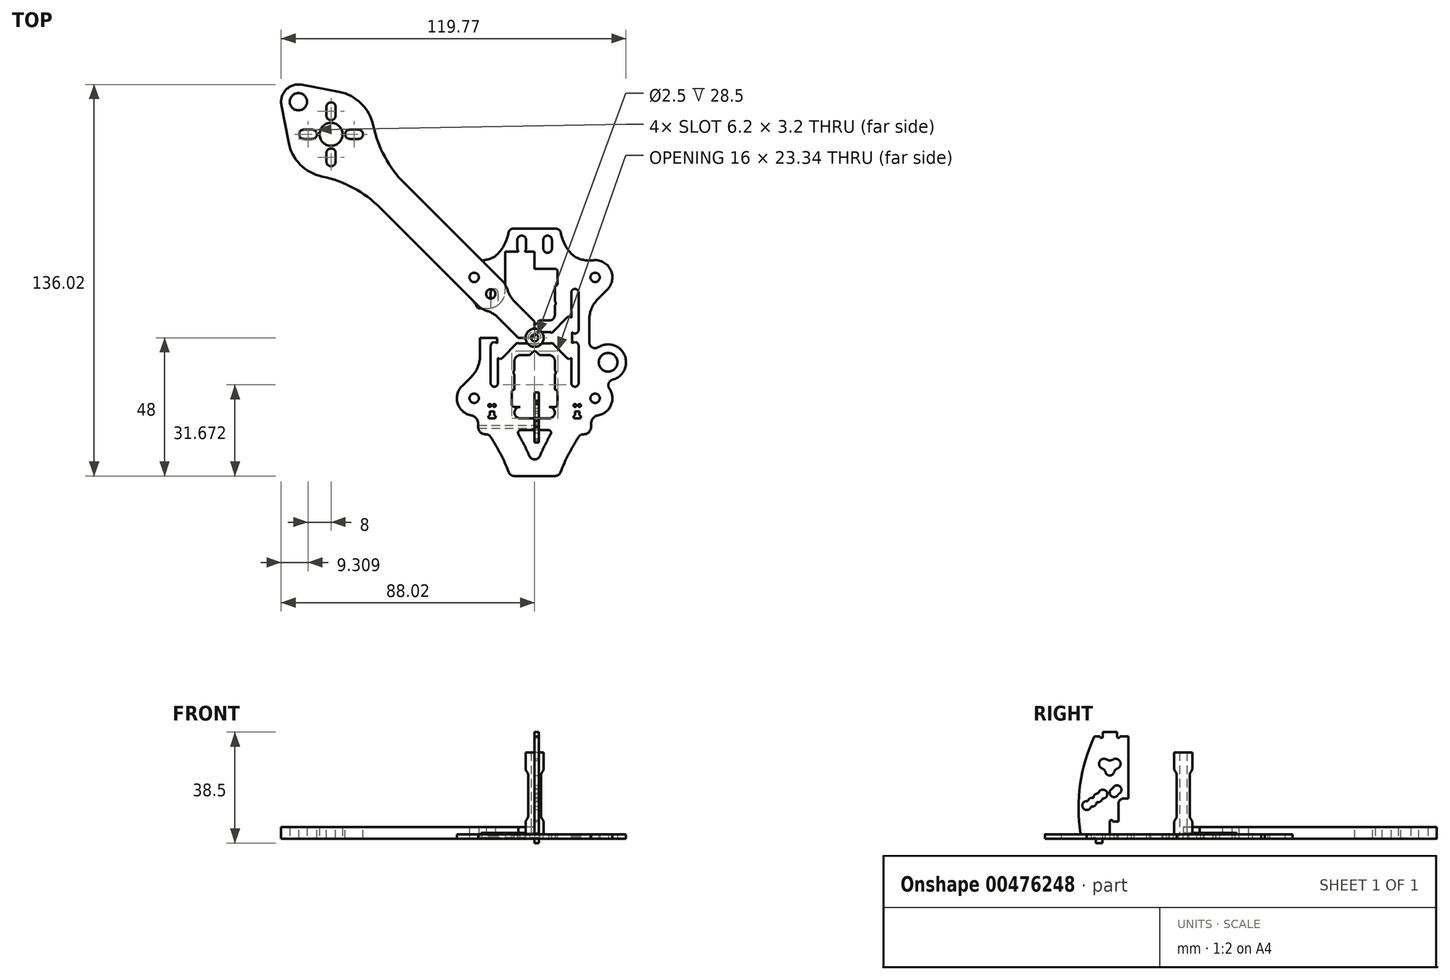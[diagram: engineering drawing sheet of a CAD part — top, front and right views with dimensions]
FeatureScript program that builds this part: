
annotation { "Feature Type Name" : "Feature", "Feature Type Description" : "" }
export const myFeature = defineFeature(function(context is Context, id is Id, definition is map)
    precondition{}
    {
        {
            var Q0;
            Q0=qCreatedBy(makeId("Top.planeOp"),FACE);
            var sketch = newSketch(context, id + "F0", { "sketchPlane" : qUnion([Q0])});
            skCircle(sketch, "E0", {"center": v(-15.25, 15.25) * mm, "radius": 2.23 * mm});
            skCircle(sketch, "E1", {"center": v(15.25, 15.25) * mm, "radius": 2.23 * mm});
            skCircle(sketch, "E2", {"center": v(15.25, -15.25) * mm, "radius": 2.23 * mm});
            skCircle(sketch, "E3", {"center": v(-15.25, -15.25) * mm, "radius": 2.23 * mm});
            skCircle(sketch, "E4", {"center": v(-21, 21) * mm, "radius": 1.63 * mm});
            skCircle(sketch, "E5.MirrorC", {"center": v(21, 21) * mm, "radius": 1.63 * mm});
            skCircle(sketch, "E6.MirrorC", {"center": v(-21, -21) * mm, "radius": 1.63 * mm});
            skCircle(sketch, "E7.MirrorC", {"center": v(21, -21) * mm, "radius": 1.63 * mm});
            skArc(sketch, "E8", {"start": v(-16.76, 25.24) * mm, "mid": v(-25.24, 25.24) * mm, "end": v(-25.24, 16.76) * mm});
            skLineSegment(sketch, "E9", {"start": v(-16.76, 25.24) * mm, "end": v(-15.56, 24.04) * mm});
            skLineSegment(sketch, "E10", {"start": v(-25.24, 16.76) * mm, "end": v(-21.93, 13.44) * mm});
            skLineSegment(sketch, "E11.MirrorCS", {"start": v(-25.24, -16.76) * mm, "end": v(-21.93, -13.44) * mm});
            skArc(sketch, "E12.MirrorCS", {"start": v(-16.76, -25.24) * mm, "mid": v(-25.24, -25.24) * mm, "end": v(-25.24, -16.76) * mm});
            skLineSegment(sketch, "E13.MirrorCS", {"start": v(-16.76, -25.24) * mm, "end": v(-15.56, -24.04) * mm});
            skLineSegment(sketch, "E14.MirrorCS", {"start": v(16.76, 25.24) * mm, "end": v(15.56, 24.04) * mm});
            skArc(sketch, "E15.MirrorCS", {"start": v(16.76, 25.24) * mm, "mid": v(25.24, 25.24) * mm, "end": v(25.24, 16.76) * mm});
            skLineSegment(sketch, "E16.MirrorCS", {"start": v(25.24, 16.76) * mm, "end": v(21.93, 13.44) * mm});
            skLineSegment(sketch, "E17.MirrorCS", {"start": v(25.24, -16.76) * mm, "end": v(21.93, -13.44) * mm});
            skArc(sketch, "E18.MirrorCS", {"start": v(16.76, -25.24) * mm, "mid": v(25.24, -25.24) * mm, "end": v(25.24, -16.76) * mm});
            skLineSegment(sketch, "E19.MirrorCS", {"start": v(16.76, -25.24) * mm, "end": v(15.56, -24.04) * mm});
            skPoint(sketch, "E20.visualSharp", {"position": v(0, 8.49) * mm});
            skPoint(sketch, "E21.visualSharp", {"position": v(0, -8.49) * mm});
            skArc(sketch, "E21.filletArc", {"start": v(15.56, -24.04) * mm, "mid": v(0, -17.6) * mm, "end": v(-15.56, -24.04) * mm});
            skLineSegment(sketch, "E22", {"start": v(-21, 21) * mm, "end": v(0, 0) * mm, "construction": true});
            skArc(sketch, "E23.filletArc", {"start": v(-15.56, 24.04) * mm, "mid": v(0, 17.6) * mm, "end": v(15.56, 24.04) * mm});
            skLineSegment(sketch, "E24", {"start": v(-19, 6.37) * mm, "end": v(-19, -6.37) * mm});
            skLineSegment(sketch, "E25.MirrorCS", {"start": v(19, 6.37) * mm, "end": v(19, -6.37) * mm});
            skLineSegment(sketch, "E26", {"start": v(0, 0) * mm, "end": v(21, -21) * mm, "construction": true});
            skLineSegment(sketch, "E27", {"start": v(21, 21) * mm, "end": v(-21, -21) * mm, "construction": true});
            skLineSegment(sketch, "E28.0", {"start": v(0.7, -7.78) * mm, "end": v(5.22, -12.3) * mm});
            skLineSegment(sketch, "E28.1", {"start": v(-12.3, 5.22) * mm, "end": v(-7.78, 0.7) * mm});
            skLineSegment(sketch, "E29.0", {"start": v(-5.22, 12.3) * mm, "end": v(-0.7, 7.78) * mm});
            skLineSegment(sketch, "E30.0", {"start": v(7.78, -0.7) * mm, "end": v(12.3, -5.22) * mm});
            skLineSegment(sketch, "E31.MirrorCS", {"start": v(5.22, 12.3) * mm, "end": v(0.7, 7.78) * mm});
            skLineSegment(sketch, "E32.MirrorCS", {"start": v(12.3, 5.22) * mm, "end": v(7.78, 0.7) * mm});
            skLineSegment(sketch, "E33.MirrorCS", {"start": v(-0.7, -7.78) * mm, "end": v(-5.22, -12.3) * mm});
            skLineSegment(sketch, "E34.MirrorCS", {"start": v(-7.78, -0.7) * mm, "end": v(-12.3, -5.22) * mm});
            skPoint(sketch, "E35.orphan", {"position": v(-3.54, -3.54) * mm});
            skPoint(sketch, "E36.orphan", {"position": v(3.54, -3.54) * mm});
            skLineSegment(sketch, "E37", {"start": v(-4.51, 14) * mm, "end": v(4.51, 14) * mm});
            skLineSegment(sketch, "E38", {"start": v(-14, 4.51) * mm, "end": v(-14, -4.51) * mm});
            skLineSegment(sketch, "E39", {"start": v(-4.51, -14) * mm, "end": v(4.51, -14) * mm});
            skLineSegment(sketch, "E40", {"start": v(14, -4.51) * mm, "end": v(14, 4.51) * mm});
            skPoint(sketch, "E41.visualSharp", {"position": v(-14, 6.93) * mm});
            skArc(sketch, "E41.filletArc", {"start": v(-12.3, 5.22) * mm, "mid": v(-13.38, 5.44) * mm, "end": v(-14, 4.51) * mm});
            skPoint(sketch, "E42.visualSharp", {"position": v(-14, -6.93) * mm});
            skArc(sketch, "E42.filletArc", {"start": v(-14, -4.51) * mm, "mid": v(-13.38, -5.44) * mm, "end": v(-12.3, -5.22) * mm});
            skPoint(sketch, "E43.visualSharp", {"position": v(-7.07, 0) * mm});
            skArc(sketch, "E43.filletArc", {"start": v(-7.78, -0.7) * mm, "mid": v(-7.49, 0) * mm, "end": v(-7.78, 0.7) * mm});
            skPoint(sketch, "E44.visualSharp", {"position": v(0, -7.07) * mm});
            skArc(sketch, "E44.filletArc", {"start": v(0.7, -7.78) * mm, "mid": v(0, -7.49) * mm, "end": v(-0.7, -7.78) * mm});
            skPoint(sketch, "E45.visualSharp", {"position": v(-6.93, -14) * mm});
            skArc(sketch, "E45.filletArc", {"start": v(-5.22, -12.3) * mm, "mid": v(-5.44, -13.38) * mm, "end": v(-4.51, -14) * mm});
            skPoint(sketch, "E46.visualSharp", {"position": v(6.93, -14) * mm});
            skArc(sketch, "E46.filletArc", {"start": v(4.51, -14) * mm, "mid": v(5.44, -13.38) * mm, "end": v(5.22, -12.3) * mm});
            skPoint(sketch, "E47.visualSharp", {"position": v(14, -6.93) * mm});
            skArc(sketch, "E47.filletArc", {"start": v(12.3, -5.22) * mm, "mid": v(13.38, -5.44) * mm, "end": v(14, -4.51) * mm});
            skPoint(sketch, "E48.visualSharp", {"position": v(14, 6.93) * mm});
            skArc(sketch, "E48.filletArc", {"start": v(14, 4.51) * mm, "mid": v(13.38, 5.44) * mm, "end": v(12.3, 5.22) * mm});
            skPoint(sketch, "E49.visualSharp", {"position": v(7.07, 0) * mm});
            skArc(sketch, "E49.filletArc", {"start": v(7.78, 0.7) * mm, "mid": v(7.49, 0) * mm, "end": v(7.78, -0.7) * mm});
            skPoint(sketch, "E50.visualSharp", {"position": v(0, 7.07) * mm});
            skArc(sketch, "E50.filletArc", {"start": v(-0.7, 7.78) * mm, "mid": v(0, 7.49) * mm, "end": v(0.7, 7.78) * mm});
            skPoint(sketch, "E51.visualSharp", {"position": v(-6.93, 14) * mm});
            skArc(sketch, "E51.filletArc", {"start": v(-4.51, 14) * mm, "mid": v(-5.44, 13.38) * mm, "end": v(-5.22, 12.3) * mm});
            skPoint(sketch, "E52.visualSharp", {"position": v(6.93, 14) * mm});
            skArc(sketch, "E52.filletArc", {"start": v(5.22, 12.3) * mm, "mid": v(5.44, 13.38) * mm, "end": v(4.51, 14) * mm});
            skPoint(sketch, "E53.visualSharp", {"position": v(-19, 10.51) * mm});
            skArc(sketch, "E53.filletArc", {"start": v(-19, 6.37) * mm, "mid": v(-19.76, 10.2) * mm, "end": v(-21.93, 13.44) * mm});
            skPoint(sketch, "E54.visualSharp", {"position": v(-19, -10.51) * mm});
            skArc(sketch, "E54.filletArc", {"start": v(-21.93, -13.44) * mm, "mid": v(-19.76, -10.2) * mm, "end": v(-19, -6.37) * mm});
            skPoint(sketch, "E55.visualSharp", {"position": v(19, -10.51) * mm});
            skArc(sketch, "E55.filletArc", {"start": v(19, -6.37) * mm, "mid": v(19.76, -10.2) * mm, "end": v(21.93, -13.44) * mm});
            skPoint(sketch, "E56.visualSharp", {"position": v(19, 10.51) * mm});
            skArc(sketch, "E56.filletArc", {"start": v(21.93, 13.44) * mm, "mid": v(19.76, 10.2) * mm, "end": v(19, 6.37) * mm});
            skSolve(sketch);
        }
        {
            var Q0;
            Q0=makeQuery(id+"F0.imprint","IMPRINT",FACE,{"disambiguationData":[TD([[makeQuery(id+"F0.imprint","IMPRINT",EDGE,{"derivedFrom":sQuery(id+"F0.wireOp",EDGE,"E0")}),-1.0]])]});
            extrude(context, id + "F1", {"entities" : qUnion([Q0]), "depth" : 1.5 * mm, "offsetDistance" : 25 * mm});
        }
        {
            var Q0;
            Q0=qCreatedBy(makeId("Top.planeOp"),FACE);
            var sketch = newSketch(context, id + "F2", { "sketchPlane" : qUnion([Q0])});
            skCircle(sketch, "E57", {"center": v(-15.25, 15.25) * mm, "radius": 1.63 * mm});
            skCircle(sketch, "E58", {"center": v(-21, 21) * mm, "radius": 1.63 * mm});
            skArc(sketch, "E59", {"start": v(-20.23, 26.95) * mm, "mid": v(-26.38, 23.65) * mm, "end": v(-25.24, 16.76) * mm});
            skLineSegment(sketch, "E60", {"start": v(-18, 7.44) * mm, "end": v(-18, 0) * mm});
            skPoint(sketch, "E61.visualSharp", {"position": v(-18, 10) * mm});
            skLineSegment(sketch, "E62", {"start": v(0, 38) * mm, "end": v(0, -38) * mm, "construction": true});
            skLineSegment(sketch, "E63.MirrorCS", {"start": v(18, 7.44) * mm, "end": v(18, 0) * mm});
            skArc(sketch, "E64.MirrorCS", {"start": v(20.23, 26.95) * mm, "mid": v(26.38, 23.65) * mm, "end": v(25.24, 16.76) * mm});
            skCircle(sketch, "E65.MirrorC", {"center": v(21, 21) * mm, "radius": 1.63 * mm});
            skCircle(sketch, "E66.MirrorC", {"center": v(15.25, 15.25) * mm, "radius": 1.63 * mm});
            skPoint(sketch, "E67.MirrorP", {"position": v(18, 10) * mm});
            skPoint(sketch, "E68.MirrorP", {"position": v(18, -10) * mm});
            skLineSegment(sketch, "E69.MirrorCS", {"start": v(18, -7.44) * mm, "end": v(18, 0) * mm});
            skLineSegment(sketch, "E70.MirrorCS", {"start": v(-18, -7.44) * mm, "end": v(-18, 0) * mm});
            skPoint(sketch, "E71.MirrorP", {"position": v(-18, -10) * mm});
            skCircle(sketch, "E72.MirrorC", {"center": v(-15.25, -15.25) * mm, "radius": 1.63 * mm});
            skCircle(sketch, "E73.MirrorC", {"center": v(-21, -21) * mm, "radius": 1.63 * mm});
            skArc(sketch, "E74.MirrorCS", {"start": v(-22.07, -26.9) * mm, "mid": v(-26.73, -22.8) * mm, "end": v(-25.24, -16.76) * mm});
            skCircle(sketch, "E75.MirrorC", {"center": v(21, -21) * mm, "radius": 1.63 * mm});
            skCircle(sketch, "E76.MirrorC", {"center": v(15.25, -15.25) * mm, "radius": 1.63 * mm});
            skArc(sketch, "E77.MirrorCS", {"start": v(22.07, -26.9) * mm, "mid": v(26.73, -22.8) * mm, "end": v(25.24, -16.76) * mm});
            skLineSegment(sketch, "E78.bottom", {"start": v(-15.6, -25.5) * mm, "end": v(-14, -25.5) * mm});
            skLineSegment(sketch, "E78.top", {"start": v(-15.6, -30.5) * mm, "end": v(-14, -30.5) * mm});
            skLineSegment(sketch, "E78.left", {"start": v(-15.6, -25.5) * mm, "end": v(-15.6, -30.5) * mm});
            skLineSegment(sketch, "E78.right", {"start": v(-14, -25.5) * mm, "end": v(-14, -30.5) * mm});
            skLineSegment(sketch, "E79.MirrorCS", {"start": v(15.6, -25.5) * mm, "end": v(14, -25.5) * mm});
            skLineSegment(sketch, "E80.MirrorCS", {"start": v(15.6, -25.5) * mm, "end": v(15.6, -30.5) * mm});
            skLineSegment(sketch, "E81.MirrorCS", {"start": v(14, -25.5) * mm, "end": v(14, -30.5) * mm});
            skLineSegment(sketch, "E82.MirrorCS", {"start": v(15.6, -30.5) * mm, "end": v(14, -30.5) * mm});
            skLineSegment(sketch, "E83", {"start": v(-25.24, -16.76) * mm, "end": v(-25.24, -16.76) * mm});
            skLineSegment(sketch, "E84", {"start": v(-21, -21) * mm, "end": v(0, 0) * mm, "construction": true});
            skLineSegment(sketch, "E85", {"start": v(-19.6, -29.86) * mm, "end": v(-19.6, -31) * mm});
            skLineSegment(sketch, "E86", {"start": v(-17.1, -33.5) * mm, "end": v(-16.97, -33.5) * mm});
            skLineSegment(sketch, "E87.MirrorCS", {"start": v(19.6, -29.86) * mm, "end": v(19.6, -31) * mm});
            skLineSegment(sketch, "E88.MirrorCS", {"start": v(17.1, -33.5) * mm, "end": v(16.97, -33.5) * mm});
            skLineSegment(sketch, "E89", {"start": v(-25.24, 16.76) * mm, "end": v(-19.46, 10.98) * mm});
            skLineSegment(sketch, "E90", {"start": v(0, 0) * mm, "end": v(-15.25, 15.25) * mm, "construction": true});
            skLineSegment(sketch, "E91.MirrorCS", {"start": v(-25.24, -16.76) * mm, "end": v(-19.46, -10.98) * mm});
            skLineSegment(sketch, "E92.MirrorCS", {"start": v(25.24, 16.76) * mm, "end": v(19.46, 10.98) * mm});
            skLineSegment(sketch, "E93.MirrorCS", {"start": v(25.24, -16.76) * mm, "end": v(19.46, -10.98) * mm});
            skLineSegment(sketch, "E94", {"start": v(-21, -21) * mm, "end": v(-70.71, -70.71) * mm, "construction": true});
            skCircle(sketch, "E95", {"center": v(-70.71, -70.71) * mm, "radius": 64.25 * mm, "construction": true});
            skArc(sketch, "E96", {"start": v(-8.47, -48) * mm, "mid": v(-11.5, -41) * mm, "end": v(-15.3, -34.4) * mm});
            skLineSegment(sketch, "E97", {"start": v(-8.47, -48) * mm, "end": v(0, -48) * mm});
            skArc(sketch, "E98.MirrorCS", {"start": v(8.47, -48) * mm, "mid": v(11.5, -41) * mm, "end": v(15.3, -34.4) * mm});
            skLineSegment(sketch, "E99.MirrorCS", {"start": v(8.47, -48) * mm, "end": v(0, -48) * mm});
            skArc(sketch, "E100", {"start": v(-20.23, 26.95) * mm, "mid": v(-12.61, 29.12) * mm, "end": v(-8.96, 36.14) * mm});
            skArc(sketch, "E101.MirrorCS", {"start": v(20.23, 26.95) * mm, "mid": v(12.61, 29.12) * mm, "end": v(8.96, 36.14) * mm});
            skPoint(sketch, "E102.visualSharp", {"position": v(-15.9, -33.5) * mm});
            skArc(sketch, "E102.filletArc", {"start": v(-15.3, -34.4) * mm, "mid": v(-16.02, -33.74) * mm, "end": v(-16.97, -33.5) * mm});
            skPoint(sketch, "E103.visualSharp", {"position": v(15.9, -33.5) * mm});
            skArc(sketch, "E103.filletArc", {"start": v(16.97, -33.5) * mm, "mid": v(16.02, -33.74) * mm, "end": v(15.3, -34.4) * mm});
            skLineSegment(sketch, "E104", {"start": v(-6.97, 38) * mm, "end": v(6.97, 38) * mm});
            skPoint(sketch, "E105.orphan", {"position": v(-8.47, 48) * mm});
            skPoint(sketch, "E106.orphan", {"position": v(8.47, 48) * mm});
            skPoint(sketch, "E107.visualSharp", {"position": v(-9, 38) * mm});
            skArc(sketch, "E107.filletArc", {"start": v(-6.97, 38) * mm, "mid": v(-8.33, 37.46) * mm, "end": v(-8.96, 36.14) * mm});
            skPoint(sketch, "E108.visualSharp", {"position": v(9, 38) * mm});
            skArc(sketch, "E108.filletArc", {"start": v(8.96, 36.14) * mm, "mid": v(8.33, 37.46) * mm, "end": v(6.97, 38) * mm});
            skPoint(sketch, "E109.visualSharp", {"position": v(-18, 9.51) * mm});
            skArc(sketch, "E109.filletArc", {"start": v(-18, 7.44) * mm, "mid": v(-18.38, 9.36) * mm, "end": v(-19.46, 10.98) * mm});
            skPoint(sketch, "E110.visualSharp", {"position": v(-18, -9.51) * mm});
            skArc(sketch, "E110.filletArc", {"start": v(-19.46, -10.98) * mm, "mid": v(-18.38, -9.36) * mm, "end": v(-18, -7.44) * mm});
            skPoint(sketch, "E111.visualSharp", {"position": v(18, 9.51) * mm});
            skArc(sketch, "E111.filletArc", {"start": v(19.46, 10.98) * mm, "mid": v(18.38, 9.36) * mm, "end": v(18, 7.44) * mm});
            skPoint(sketch, "E112.visualSharp", {"position": v(18, -9.51) * mm});
            skArc(sketch, "E112.filletArc", {"start": v(18, -7.44) * mm, "mid": v(18.38, -9.36) * mm, "end": v(19.46, -10.98) * mm});
            skArc(sketch, "E113", {"start": v(-19.6, -29.86) * mm, "mid": v(-20.3, -27.93) * mm, "end": v(-22.07, -26.9) * mm});
            skPoint(sketch, "E114.visualSharp", {"position": v(-19.6, -33.5) * mm});
            skArc(sketch, "E114.filletArc", {"start": v(-19.6, -31) * mm, "mid": v(-18.87, -32.77) * mm, "end": v(-17.1, -33.5) * mm});
            skArc(sketch, "E115.MirrorCS", {"start": v(19.6, -29.86) * mm, "mid": v(20.3, -27.93) * mm, "end": v(22.07, -26.9) * mm});
            skPoint(sketch, "E116.visualSharp", {"position": v(19.6, -33.5) * mm});
            skArc(sketch, "E116.filletArc", {"start": v(17.1, -33.5) * mm, "mid": v(18.87, -32.77) * mm, "end": v(19.6, -31) * mm});
            skSolve(sketch);
        }
        {
            var Q0;
            Q0=makeQuery(id+"F2.imprint","IMPRINT",FACE,{"disambiguationData":[TD([[makeQuery(id+"F2.imprint","IMPRINT",EDGE,{"derivedFrom":sQuery(id+"F2.wireOp",EDGE,"E57")}),-1.0]])]});
            extrude(context, id + "F3", {"entities" : qUnion([Q0]), "depth" : 1.5 * mm});
        }
        {
            var Q0;
            Q0=makeQuery(id+"F3.opExtrude","CAP_FACE",FACE,{"disambiguationData":[OSD([sQuery(id+"F2.wireOp",EDGE,"E57"),sQuery(id+"F2.wireOp",EDGE,"jFPTTxz4-jLXj-DDCv-FC09-USVAbM95QFUD"),sQuery(id+"F2.wireOp",EDGE,"E58"),sQuery(id+"F2.wireOp",EDGE,"E59"),sQuery(id+"F2.wireOp",EDGE,"E60"),sQuery(id+"F2.wireOp",EDGE,"OV2Wl9yg-sUyD-2Hj2-rkXj-MTIEYF9VZsJK"),sQuery(id+"F2.wireOp",EDGE,"91e39d24-f0d0-409c-99ef-685c742f9300.filletArc"),sQuery(id+"F2.wireOp",EDGE,"E61.filletArc"),sQuery(id+"F2.wireOp",EDGE,"2RSG9yHZ-WQqx-c2xK-pqDh-UdEIjaxC7IlA"),sQuery(id+"F2.wireOp",EDGE,"4rgxPuH5-7xbP-ZsFa-2w6e-7YXQlRziYjOP"),sQuery(id+"F2.wireOp",EDGE,"aAb2sQRX-3QeW-SLoE-m21K-AacbavdIfjy6"),sQuery(id+"F2.wireOp",EDGE,"7c283ec5-88dc-4330-9acd-45fa73696fd10.MirrorCS"),sQuery(id+"F2.wireOp",EDGE,"7c283ec5-88dc-4330-9acd-45fa73696fd11.MirrorCS"),sQuery(id+"F2.wireOp",EDGE,"E63.MirrorCS"),sQuery(id+"F2.wireOp",EDGE,"E64.MirrorCS"),sQuery(id+"F2.wireOp",EDGE,"E65.MirrorC"),sQuery(id+"F2.wireOp",EDGE,"7c283ec5-88dc-4330-9acd-45fa73696fd112.MirrorC"),sQuery(id+"F2.wireOp",EDGE,"E66.MirrorC"),sQuery(id+"F2.wireOp",EDGE,"7c283ec5-88dc-4330-9acd-45fa73696fd114.MirrorCS"),sQuery(id+"F2.wireOp",EDGE,"7c283ec5-88dc-4330-9acd-45fa73696fd116.MirrorCS"),sQuery(id+"F2.wireOp",EDGE,"77becaeb-8b8b-4dc1-b250-45090536f0a20.MirrorCS"),sQuery(id+"F2.wireOp",EDGE,"26ce58a3-4cb5-4f15-a1e7-5b8d20efb5c40.MirrorCS"),sQuery(id+"F2.wireOp",EDGE,"9822711c-84ae-4c2d-bbd4-b3a60979fe173.MirrorCS"),sQuery(id+"F2.wireOp",EDGE,"9822711c-84ae-4c2d-bbd4-b3a60979fe174.MirrorCS"),sQuery(id+"F2.wireOp",EDGE,"E69.MirrorCS"),sQuery(id+"F2.wireOp",EDGE,"9822711c-84ae-4c2d-bbd4-b3a60979fe176.MirrorCS"),sQuery(id+"F2.wireOp",EDGE,"4a2114cf-ddcc-4bd1-b273-f588f7a722dc0.MirrorCS"),sQuery(id+"F2.wireOp",EDGE,"4a2114cf-ddcc-4bd1-b273-f588f7a722dc1.MirrorCS"),sQuery(id+"F2.wireOp",EDGE,"4a2114cf-ddcc-4bd1-b273-f588f7a722dc2.MirrorCS"),sQuery(id+"F2.wireOp",EDGE,"E70.MirrorCS"),sQuery(id+"F2.wireOp",EDGE,"E72.MirrorC"),sQuery(id+"F2.wireOp",EDGE,"E73.MirrorC"),sQuery(id+"F2.wireOp",EDGE,"E74.MirrorCS"),sQuery(id+"F2.wireOp",EDGE,"E75.MirrorC"),sQuery(id+"F2.wireOp",EDGE,"E76.MirrorC"),sQuery(id+"F2.wireOp",EDGE,"5bfa031d-9f72-4db7-bc0c-70e661b370ed0.MirrorC"),sQuery(id+"F2.wireOp",EDGE,"6425a8bc-ce2c-4a8b-8028-989707d169630.MirrorC"),sQuery(id+"F2.wireOp",EDGE,"E77.MirrorCS"),sQuery(id+"F2.wireOp",EDGE,"b8184357-9e1d-4d76-b8cc-bd6e0700e5e00.MirrorCS"),sQuery(id+"F2.wireOp",EDGE,"32760b4d-dda8-4da2-a85d-3a466e5e60c60.MirrorCS"),sQuery(id+"F2.wireOp",EDGE,"3608dae1-eb2e-4dc6-816e-64e42f027ba40.MirrorCS"),sQuery(id+"F2.wireOp",EDGE,"ed51ebd1-3bfc-4bb5-896a-a1a15a693a9f0.MirrorCS"),sQuery(id+"F2.wireOp",EDGE,"c6e026e1-fe79-4e24-8aee-e9c260e0377b0.MirrorCS"),sQuery(id+"F2.wireOp",EDGE,"681415bc-d1ca-493e-a100-2ccd6f0434aa0.MirrorCS"),sQuery(id+"F2.wireOp",EDGE,"E78.bottom"),sQuery(id+"F2.wireOp",EDGE,"E78.top"),sQuery(id+"F2.wireOp",EDGE,"E78.left"),sQuery(id+"F2.wireOp",EDGE,"E78.right"),sQuery(id+"F2.wireOp",EDGE,"E79.MirrorCS"),sQuery(id+"F2.wireOp",EDGE,"E80.MirrorCS"),sQuery(id+"F2.wireOp",EDGE,"E81.MirrorCS"),sQuery(id+"F2.wireOp",EDGE,"E82.MirrorCS"),sQuery(id+"F2.wireOp",EDGE,"VBkXurKH-HzS8-dzkn-LxKA-4I1jdE3c4Em0"),sQuery(id+"F2.wireOp",EDGE,"b7184078-a67c-4706-b7f2-105a01179b9c.filletArc"),sQuery(id+"F2.wireOp",EDGE,"b7237c02-60dc-40f2-a213-8a94564c20be0.MirrorCS"),sQuery(id+"F2.wireOp",EDGE,"bdf4f6a4-df0c-4300-a64c-7dace4eac6310.MirrorCS"),sQuery(id+"F2.wireOp",EDGE,"ee7ddf88-5d4a-4064-9a04-f45d6847952f0.MirrorCS"),sQuery(id+"F2.wireOp",EDGE,"de45aa2e-6ca1-40a2-bc78-a00ece19e9440.MirrorCS"),sQuery(id+"F2.wireOp",EDGE,"1337a31e-3a8f-42fa-aa43-79b785e411150.MirrorCS"),sQuery(id+"F2.wireOp",EDGE,"daa37f43-5825-406c-9ff9-18d668761be80.MirrorCS")])],"isStart":true});
            var sketch = newSketch(context, id + "F4", { "sketchPlane" : qUnion([Q0])});
            skCircle(sketch, "E117", {"center": v(-15.6, 30) * mm, "radius": 0.5 * mm});
            skCircle(sketch, "E118", {"center": v(-14, 30) * mm, "radius": 0.5 * mm});
            skCircle(sketch, "E119", {"center": v(-15.6, 26) * mm, "radius": 0.5 * mm});
            skCircle(sketch, "E120", {"center": v(-14, 26) * mm, "radius": 0.5 * mm});
            skCircle(sketch, "E121.MirrorC", {"center": v(14, 26) * mm, "radius": 0.5 * mm});
            skCircle(sketch, "E122.MirrorC", {"center": v(15.6, 30) * mm, "radius": 0.5 * mm});
            skCircle(sketch, "E123.MirrorC", {"center": v(14, 30) * mm, "radius": 0.5 * mm});
            skCircle(sketch, "E124.MirrorC", {"center": v(15.6, 26) * mm, "radius": 0.5 * mm});
            skSolve(sketch);
        }
        {
            var Q0;
            Q0=qSketchRegion(id+"F4",true);
            extrude(context, id + "F5", {"entities" : qUnion([Q0]), "operationType" : NewBodyOperationType.REMOVE, "oppositeDirection" : true, "depth" : 25 * mm});
        }
        {
            var Q0;
            Q0=qCreatedBy(makeId("Top.planeOp"),FACE);
            var sketch = newSketch(context, id + "F6", { "sketchPlane" : qUnion([Q0])});
            skCircle(sketch, "E125", {"center": v(-15.25, 15.25) * mm, "radius": 1.63 * mm});
            skCircle(sketch, "E126", {"center": v(-21, 21) * mm, "radius": 1.63 * mm});
            skLineSegment(sketch, "E127", {"start": v(0, 0) * mm, "end": v(-70.71, 70.71) * mm, "construction": true});
            skLineSegment(sketch, "E128", {"start": v(-11, 19.5) * mm, "end": v(-45.15, 53.63) * mm});
            skLineSegment(sketch, "E129", {"start": v(-5.66, 0) * mm, "end": v(0, 0) * mm});
            skLineSegment(sketch, "E130", {"start": v(0, 0) * mm, "end": v(0, 5.66) * mm});
            skArc(sketch, "E131", {"start": v(-85.45, 67.9) * mm, "mid": v(-81.4, 60.2) * mm, "end": v(-73.77, 56.03) * mm});
            skArc(sketch, "E132", {"start": v(-80.9, 87.92) * mm, "mid": v(-86.27, 86.27) * mm, "end": v(-87.92, 80.9) * mm});
            skCircle(sketch, "E133", {"center": v(-82.02, 82.02) * mm, "radius": 3 * mm});
            skLineSegment(sketch, "E134", {"start": v(-70.71, 70.71) * mm, "end": v(-82.02, 82.02) * mm, "construction": true});
            skPoint(sketch, "E135.visualSharp", {"position": v(-76.57, 84.52) * mm});
            skPoint(sketch, "E136.visualSharp", {"position": v(-84.52, 76.57) * mm});
            skCircle(sketch, "E137", {"center": v(-70.71, 70.71) * mm, "radius": 64.25 * mm, "construction": true});
            skArc(sketch, "E138.trimOffspring", {"start": v(-56.03, 73.77) * mm, "mid": v(-60.2, 81.4) * mm, "end": v(-67.9, 85.45) * mm});
            skPoint(sketch, "E139.visualSharp", {"position": v(-56.75, 65.23) * mm});
            skArc(sketch, "E139.filletArc", {"start": v(-56.03, 73.77) * mm, "mid": v(-52.06, 62.9) * mm, "end": v(-45.15, 53.63) * mm});
            skCircle(sketch, "E140", {"center": v(-70.71, 70.71) * mm, "radius": 4 * mm});
            skLineSegment(sketch, "E141.trimOffspring", {"start": v(-19.5, 11) * mm, "end": v(-53.63, 45.15) * mm});
            skArc(sketch, "E142.trimOffspring", {"start": v(-19.5, 11) * mm, "mid": v(-18.3, 10.08) * mm, "end": v(-16.9, 9.48) * mm});
            skLineSegment(sketch, "E143", {"start": v(-5.66, 0) * mm, "end": v(-12.6, 6.94) * mm});
            skLineSegment(sketch, "E144", {"start": v(-6.94, 12.6) * mm, "end": v(0, 5.66) * mm});
            skArc(sketch, "E145.trimOffspring", {"start": v(-9.48, 16.9) * mm, "mid": v(-10.08, 18.3) * mm, "end": v(-11, 19.5) * mm});
            skPoint(sketch, "E146.orphan", {"position": v(0, 8.49) * mm});
            skPoint(sketch, "E147.visualSharp", {"position": v(-14.92, 9.26) * mm});
            skArc(sketch, "E147.filletArc", {"start": v(-12.6, 6.94) * mm, "mid": v(-14.6, 8.49) * mm, "end": v(-16.9, 9.48) * mm});
            skPoint(sketch, "E148.visualSharp", {"position": v(-9.26, 14.92) * mm});
            skArc(sketch, "E148.filletArc", {"start": v(-9.48, 16.9) * mm, "mid": v(-8.49, 14.6) * mm, "end": v(-6.94, 12.6) * mm});
            skArc(sketch, "E149.MirrorCS", {"start": v(-73.77, 56.03) * mm, "mid": v(-62.9, 52.06) * mm, "end": v(-53.63, 45.15) * mm});
            skLineSegment(sketch, "E150", {"start": v(-87.92, 80.9) * mm, "end": v(-85.45, 67.9) * mm});
            skLineSegment(sketch, "E151", {"start": v(-80.9, 87.92) * mm, "end": v(-67.9, 85.45) * mm});
            skSolve(sketch);
        }
        {
            var Q0;
            Q0=qSketchRegion(id+"F6",true);
            extrude(context, id + "F7", {"entities" : qUnion([Q0]), "depth" : 4 * mm});
        }
        {
            var Q0;
            Q0=makeQuery(id+"F7.opExtrude","CAP_FACE",FACE,{"disambiguationData":[OSD([sQuery(id+"F6.wireOp",EDGE,"ELmgnBSW-vcTX-69ba-dwwi-cACzyNvr3Jda"),sQuery(id+"F6.wireOp",EDGE,"E125"),sQuery(id+"F6.wireOp",EDGE,"E126"),sQuery(id+"F6.wireOp",EDGE,"wzC1F6xg-fGIV-3KpO-c9gR-K1YJSPa7NM8s"),sQuery(id+"F6.wireOp",EDGE,"E128"),sQuery(id+"F6.wireOp",EDGE,"FoUFOdND-4TSw-zWgQ-ILiy-lV2VMV41Ndkk"),sQuery(id+"F6.wireOp",EDGE,"gZyNtGtT-cGv0-NfnX-XPpx-gTdD2O9JXBFj"),sQuery(id+"F6.wireOp",EDGE,"AxQfXuDg-QIAQ-o6Jz-UGCb-lciMLiFu8Ysp"),sQuery(id+"F6.wireOp",EDGE,"495c5933-9560-4cef-81c8-4e8a0d039e08.trimOffspring"),sQuery(id+"F6.wireOp",EDGE,"E129"),sQuery(id+"F6.wireOp",EDGE,"E130"),sQuery(id+"F6.wireOp",EDGE,"ef546a75-4e02-40f2-ac6e-af8522daafdd.filletArc"),sQuery(id+"F6.wireOp",EDGE,"2512e942-d075-422c-a12b-7db6a64d2190.filletArc"),sQuery(id+"F6.wireOp",EDGE,"E131"),sQuery(id+"F6.wireOp",EDGE,"E132"),sQuery(id+"F6.wireOp",EDGE,"E133"),sQuery(id+"F6.wireOp",EDGE,"E135.filletArc"),sQuery(id+"F6.wireOp",EDGE,"E136.filletArc"),sQuery(id+"F6.wireOp",EDGE,"E138.trimOffspring"),sQuery(id+"F6.wireOp",EDGE,"E139.filletArc"),sQuery(id+"F6.wireOp",EDGE,"abeb74fd-95f9-49b4-a37d-9e8ca5098ea8.filletArc"),sQuery(id+"F6.wireOp",EDGE,"E140")])],"isStart":false});
            var sketch = newSketch(context, id + "F8", { "sketchPlane" : qUnion([Q0])});
            skLineSegment(sketch, "E152", {"start": v(-70.71, 70.71) * mm, "end": v(-64.21, 70.71) * mm, "construction": true});
            skLineSegment(sketch, "E153", {"start": v(-70.71, 70.71) * mm, "end": v(0, 0) * mm, "construction": true});
            skLineSegment(sketch, "E154", {"start": v(-64.21, 70.71) * mm, "end": v(-61.21, 70.71) * mm, "construction": true});
            skArc(sketch, "E155.0.startCap", {"start": v(-64.21, 69.11) * mm, "mid": v(-65.81, 70.71) * mm, "end": v(-64.21, 72.31) * mm});
            skArc(sketch, "E155.0.endCap", {"start": v(-61.21, 72.31) * mm, "mid": v(-59.61, 70.71) * mm, "end": v(-61.21, 69.11) * mm});
            skLineSegment(sketch, "E155.0.left", {"start": v(-64.21, 72.31) * mm, "end": v(-61.21, 72.31) * mm});
            skLineSegment(sketch, "E155.0.right", {"start": v(-64.21, 69.11) * mm, "end": v(-61.21, 69.11) * mm});
            skLineSegment(sketch, "E156.1.0", {"start": v(-72.31, 77.21) * mm, "end": v(-72.31, 80.21) * mm});
            skArc(sketch, "E156.1.1", {"start": v(-69.11, 77.21) * mm, "mid": v(-70.71, 75.61) * mm, "end": v(-72.31, 77.21) * mm});
            skLineSegment(sketch, "E156.1.2", {"start": v(-69.11, 77.21) * mm, "end": v(-69.11, 80.21) * mm});
            skArc(sketch, "E156.1.3", {"start": v(-72.31, 80.21) * mm, "mid": v(-70.71, 81.81) * mm, "end": v(-69.11, 80.21) * mm});
            skLineSegment(sketch, "E156.2.0", {"start": v(-77.21, 69.11) * mm, "end": v(-80.21, 69.11) * mm});
            skArc(sketch, "E156.2.1", {"start": v(-77.21, 72.31) * mm, "mid": v(-75.61, 70.71) * mm, "end": v(-77.21, 69.11) * mm});
            skLineSegment(sketch, "E156.2.2", {"start": v(-77.21, 72.31) * mm, "end": v(-80.21, 72.31) * mm});
            skArc(sketch, "E156.2.3", {"start": v(-80.21, 69.11) * mm, "mid": v(-81.81, 70.71) * mm, "end": v(-80.21, 72.31) * mm});
            skLineSegment(sketch, "E156.3.0", {"start": v(-69.11, 64.21) * mm, "end": v(-69.11, 61.21) * mm});
            skArc(sketch, "E156.3.1", {"start": v(-72.31, 64.21) * mm, "mid": v(-70.71, 65.81) * mm, "end": v(-69.11, 64.21) * mm});
            skLineSegment(sketch, "E156.3.2", {"start": v(-72.31, 64.21) * mm, "end": v(-72.31, 61.21) * mm});
            skArc(sketch, "E156.3.3", {"start": v(-69.11, 61.21) * mm, "mid": v(-70.71, 59.61) * mm, "end": v(-72.31, 61.21) * mm});
            skPoint(sketch, "E156.center", {"position": v(-70.71, 70.71) * mm});
            skSolve(sketch);
        }
        {
            var Q0;
            Q0=qSketchRegion(id+"F8",true);
            extrude(context, id + "F9", {"entities" : qUnion([Q0]), "operationType" : NewBodyOperationType.REMOVE, "oppositeDirection" : true, "depth" : 25 * mm});
        }
        {
            var Q0;
            Q0=qCreatedBy(makeId("Top.planeOp"),FACE);
            var sketch = newSketch(context, id + "F10", { "sketchPlane" : qUnion([Q0])});
            skCircle(sketch, "E157", {"center": v(-21, 21) * mm, "radius": 1.65 * mm});
            skLineSegment(sketch, "E158", {"start": v(-23.83, 18.17) * mm, "end": v(-20.93, 15.27) * mm});
            skLineSegment(sketch, "E159", {"start": v(-21, 21) * mm, "end": v(0, 0) * mm, "construction": true});
            skLineSegment(sketch, "E160", {"start": v(-18, 8.2) * mm, "end": v(-18, 0) * mm});
            skPoint(sketch, "E161.visualSharp", {"position": v(-18, 12.34) * mm});
            skArc(sketch, "E161.filletArc", {"start": v(-18, 8.2) * mm, "mid": v(-18.76, 12.03) * mm, "end": v(-20.93, 15.27) * mm});
            skLineSegment(sketch, "E162", {"start": v(0, 0) * mm, "end": v(0, 0) * mm});
            skLineSegment(sketch, "E163.MirrorCS", {"start": v(18, 8.2) * mm, "end": v(18, 0) * mm});
            skPoint(sketch, "E164.MirrorP", {"position": v(18, 12.34) * mm});
            skLineSegment(sketch, "E165.MirrorCS", {"start": v(23.83, 18.17) * mm, "end": v(20.93, 15.27) * mm});
            skCircle(sketch, "E166.MirrorC", {"center": v(21, 21) * mm, "radius": 1.65 * mm});
            skLineSegment(sketch, "E167.MirrorCS", {"start": v(21, 21) * mm, "end": v(0, 0) * mm, "construction": true});
            skArc(sketch, "E168.MirrorCS", {"start": v(18, 8.2) * mm, "mid": v(18.76, 12.03) * mm, "end": v(20.93, 15.27) * mm});
            skLineSegment(sketch, "E169.MirrorCS", {"start": v(0, 36) * mm, "end": v(0, 0) * mm, "construction": true});
            skArc(sketch, "E170.MirrorCS", {"start": v(-18, -8.2) * mm, "mid": v(-18.76, -12.03) * mm, "end": v(-20.93, -15.27) * mm});
            skLineSegment(sketch, "E171.MirrorCS", {"start": v(-18, -8.2) * mm, "end": v(-18, 0) * mm});
            skLineSegment(sketch, "E172.MirrorCS", {"start": v(18, -8.2) * mm, "end": v(18, 0) * mm});
            skArc(sketch, "E173.MirrorCS", {"start": v(18, -8.2) * mm, "mid": v(18.76, -12.03) * mm, "end": v(20.93, -15.27) * mm});
            skLineSegment(sketch, "E174.MirrorCS", {"start": v(23.83, -18.17) * mm, "end": v(20.93, -15.27) * mm});
            skLineSegment(sketch, "E175.MirrorCS", {"start": v(-23.83, -18.17) * mm, "end": v(-20.93, -15.27) * mm});
            skArc(sketch, "E176.MirrorCS", {"start": v(23.83, -23.83) * mm, "mid": v(25, -21) * mm, "end": v(23.83, -18.17) * mm});
            skCircle(sketch, "E177.MirrorC", {"center": v(-21, -21) * mm, "radius": 1.65 * mm});
            skCircle(sketch, "E178.MirrorC", {"center": v(21, -21) * mm, "radius": 1.65 * mm});
            skLineSegment(sketch, "E179.bottom", {"start": v(-15.6, -23) * mm, "end": v(-14, -23) * mm});
            skLineSegment(sketch, "E179.top", {"start": v(-15.6, -28) * mm, "end": v(-14, -28) * mm});
            skLineSegment(sketch, "E179.left", {"start": v(-15.6, -23) * mm, "end": v(-15.6, -28) * mm});
            skLineSegment(sketch, "E179.right", {"start": v(-14, -23) * mm, "end": v(-14, -28) * mm});
            skLineSegment(sketch, "E180.MirrorCS", {"start": v(15.6, -28) * mm, "end": v(14, -28) * mm});
            skLineSegment(sketch, "E181.MirrorCS", {"start": v(14, -23) * mm, "end": v(14, -28) * mm});
            skLineSegment(sketch, "E182.MirrorCS", {"start": v(15.6, -23) * mm, "end": v(15.6, -28) * mm});
            skLineSegment(sketch, "E183.MirrorCS", {"start": v(15.6, -23) * mm, "end": v(14, -23) * mm});
            skLineSegment(sketch, "E184", {"start": v(0, 0) * mm, "end": v(-70.71, -70.71) * mm, "construction": true});
            skCircle(sketch, "E185", {"center": v(-70.71, -70.71) * mm, "radius": 64.25 * mm, "construction": true});
            skArc(sketch, "E186", {"start": v(-10.95, -42) * mm, "mid": v(-16.62, -32.37) * mm, "end": v(-23.83, -23.83) * mm});
            skArc(sketch, "E187", {"start": v(-23.83, -23.83) * mm, "mid": v(-25, -21) * mm, "end": v(-23.83, -18.17) * mm});
            skArc(sketch, "E188.MirrorCS", {"start": v(10.95, -42) * mm, "mid": v(16.62, -32.37) * mm, "end": v(23.83, -23.83) * mm});
            skLineSegment(sketch, "E189", {"start": v(-10.95, -42) * mm, "end": v(-8.74, -42) * mm});
            skLineSegment(sketch, "E190.trimOffspring", {"start": v(8.74, -42) * mm, "end": v(10.95, -42) * mm});
            skLineSegment(sketch, "E191", {"start": v(-3.75, 27.5) * mm, "end": v(-3.75, 25) * mm, "construction": true});
            skArc(sketch, "E192.0.startCap", {"start": v(-5, 27.5) * mm, "mid": v(-3.75, 28.75) * mm, "end": v(-2.5, 27.5) * mm});
            skArc(sketch, "E192.0.endCap", {"start": v(-2.5, 25) * mm, "mid": v(-3.75, 23.75) * mm, "end": v(-5, 25) * mm});
            skLineSegment(sketch, "E192.0.left", {"start": v(-2.5, 27.5) * mm, "end": v(-2.5, 25) * mm});
            skLineSegment(sketch, "E192.0.right", {"start": v(-5, 27.5) * mm, "end": v(-5, 25) * mm});
            skLineSegment(sketch, "E193.MirrorCS", {"start": v(5, 27.5) * mm, "end": v(5, 25) * mm});
            skArc(sketch, "E194.MirrorCS", {"start": v(5, 27.5) * mm, "mid": v(3.75, 28.75) * mm, "end": v(2.5, 27.5) * mm});
            skArc(sketch, "E195.MirrorCS", {"start": v(2.5, 25) * mm, "mid": v(3.75, 23.75) * mm, "end": v(5, 25) * mm});
            skLineSegment(sketch, "E196.MirrorCS", {"start": v(2.5, 27.5) * mm, "end": v(2.5, 25) * mm});
            skLineSegment(sketch, "E197.MirrorCS", {"start": v(3.75, 27.5) * mm, "end": v(3.75, 25) * mm, "construction": true});
            skLineSegment(sketch, "E198", {"start": v(-7.15, 38) * mm, "end": v(7.15, 38) * mm});
            skArc(sketch, "E199", {"start": v(-23.83, 18.17) * mm, "mid": v(-24.77, 22.33) * mm, "end": v(-21.42, 24.98) * mm});
            skArc(sketch, "E200", {"start": v(23.83, 18.17) * mm, "mid": v(24.77, 22.33) * mm, "end": v(21.42, 24.98) * mm});
            skArc(sketch, "E201", {"start": v(-21.42, 24.98) * mm, "mid": v(-13.38, 28.63) * mm, "end": v(-9.12, 36.36) * mm});
            skArc(sketch, "E202.MirrorCS", {"start": v(21.42, 24.98) * mm, "mid": v(13.38, 28.63) * mm, "end": v(9.12, 36.36) * mm});
            skArc(sketch, "E203", {"start": v(8.74, -42) * mm, "mid": v(0, -35.03) * mm, "end": v(-8.74, -42) * mm});
            skPoint(sketch, "E204.visualSharp", {"position": v(-8.91, 38) * mm});
            skArc(sketch, "E204.filletArc", {"start": v(-7.15, 38) * mm, "mid": v(-8.43, 37.54) * mm, "end": v(-9.12, 36.36) * mm});
            skPoint(sketch, "E205.visualSharp", {"position": v(8.91, 38) * mm});
            skArc(sketch, "E205.filletArc", {"start": v(9.12, 36.36) * mm, "mid": v(8.43, 37.54) * mm, "end": v(7.15, 38) * mm});
            skArc(sketch, "E206.0.1.0", {"start": v(2.5, 32) * mm, "mid": v(3.75, 30.75) * mm, "end": v(5, 32) * mm});
            skLineSegment(sketch, "E206.0.1.1", {"start": v(3.75, 34.5) * mm, "end": v(3.75, 32) * mm, "construction": true});
            skArc(sketch, "E206.0.1.2", {"start": v(5, 34.5) * mm, "mid": v(3.75, 35.75) * mm, "end": v(2.5, 34.5) * mm});
            skLineSegment(sketch, "E206.0.1.3", {"start": v(5, 34.5) * mm, "end": v(5, 32) * mm});
            skLineSegment(sketch, "E206.0.1.4", {"start": v(-2.5, 34.5) * mm, "end": v(-2.5, 32) * mm});
            skLineSegment(sketch, "E206.0.1.5", {"start": v(-3.75, 34.5) * mm, "end": v(-3.75, 32) * mm, "construction": true});
            skArc(sketch, "E206.0.1.6", {"start": v(-2.5, 32) * mm, "mid": v(-3.75, 30.75) * mm, "end": v(-5, 32) * mm});
            skLineSegment(sketch, "E206.0.1.7", {"start": v(2.5, 34.5) * mm, "end": v(2.5, 32) * mm});
            skLineSegment(sketch, "E206.0.1.8", {"start": v(-5, 34.5) * mm, "end": v(-5, 32) * mm});
            skArc(sketch, "E206.0.1.9", {"start": v(-5, 34.5) * mm, "mid": v(-3.75, 35.75) * mm, "end": v(-2.5, 34.5) * mm});
            skLineSegment(sketch, "E206.direction1", {"start": v(-5, 25) * mm, "end": v(20, 25) * mm, "construction": true});
            skLineSegment(sketch, "E206.direction2", {"start": v(-5, 25) * mm, "end": v(-5, 32) * mm, "construction": true});
            skSolve(sketch);
        }
        {
            var Q0;
            Q0=makeQuery(id+"F10.imprint","IMPRINT",FACE,{"disambiguationData":[TD([[makeQuery(id+"F10.imprint","IMPRINT",EDGE,{"derivedFrom":sQuery(id+"F10.wireOp",EDGE,"E157")}),-1.0]])]});
            extrude(context, id + "F11", {"entities" : qUnion([Q0]), "depth" : 1.5 * mm});
        }
        {
            var Q0;
            Q0=makeQuery(id+"F11.opExtrude","CAP_FACE",FACE,{"disambiguationData":[OSD([sQuery(id+"F10.wireOp",EDGE,"E157"),sQuery(id+"F10.wireOp",EDGE,"C1XNVG7k-0FuO-DmIR-nKNt-iijcf70ywYW7"),sQuery(id+"F10.wireOp",EDGE,"1JmxdRkD-XWPe-tDd6-sWuO-UiO5tpgJbU8n"),sQuery(id+"F10.wireOp",EDGE,"qC2pTZaY-QVpN-GFV0-oAhF-SKeQF19ME5D9"),sQuery(id+"F10.wireOp",EDGE,"E158"),sQuery(id+"F10.wireOp",EDGE,"E160"),sQuery(id+"F10.wireOp",EDGE,"E161.filletArc"),sQuery(id+"F10.wireOp",EDGE,"E163.MirrorCS"),sQuery(id+"F10.wireOp",EDGE,"7443f5ac-ebe8-482a-814f-4fc3a6a16acd2.MirrorCS"),sQuery(id+"F10.wireOp",EDGE,"E165.MirrorCS"),sQuery(id+"F10.wireOp",EDGE,"7443f5ac-ebe8-482a-814f-4fc3a6a16acd4.MirrorCS"),sQuery(id+"F10.wireOp",EDGE,"E166.MirrorC"),sQuery(id+"F10.wireOp",EDGE,"7443f5ac-ebe8-482a-814f-4fc3a6a16acd6.MirrorCS"),sQuery(id+"F10.wireOp",EDGE,"E168.MirrorCS"),sQuery(id+"F10.wireOp",EDGE,"E170.MirrorCS"),sQuery(id+"F10.wireOp",EDGE,"E171.MirrorCS"),sQuery(id+"F10.wireOp",EDGE,"E172.MirrorCS"),sQuery(id+"F10.wireOp",EDGE,"E173.MirrorCS"),sQuery(id+"F10.wireOp",EDGE,"E174.MirrorCS"),sQuery(id+"F10.wireOp",EDGE,"E175.MirrorCS"),sQuery(id+"F10.wireOp",EDGE,"920d5ffd-3ccc-4f48-bb8e-6c259681e9ea0.MirrorCS"),sQuery(id+"F10.wireOp",EDGE,"E176.MirrorCS"),sQuery(id+"F10.wireOp",EDGE,"6d739943-ed94-4d6a-83af-c7ee9b53e6000.MirrorCS"),sQuery(id+"F10.wireOp",EDGE,"92157b26-c4a0-4e89-9586-dcc7775d5ddd0.MirrorCS"),sQuery(id+"F10.wireOp",EDGE,"E177.MirrorC"),sQuery(id+"F10.wireOp",EDGE,"E178.MirrorC"),sQuery(id+"F10.wireOp",EDGE,"6LLzlCl9-pIkG-ylEb-rQc8-LpSHkL36GfJh"),sQuery(id+"F10.wireOp",EDGE,"BRovLQjg-58oc-8yov-hL1k-GmZUxygz8b3U"),sQuery(id+"F10.wireOp",EDGE,"45a8d127-23e0-4cab-910c-54c4c990bd860.MirrorCS"),sQuery(id+"F10.wireOp",EDGE,"s5xo5Asv-idW3-iZUK-O8kW-0OEmwKlhXYxH"),sQuery(id+"F10.wireOp",EDGE,"3ba12d3b-7b13-4584-9ad2-bd2aa17df9f10.MirrorCS"),sQuery(id+"F10.wireOp",EDGE,"E179.bottom"),sQuery(id+"F10.wireOp",EDGE,"E179.top"),sQuery(id+"F10.wireOp",EDGE,"E179.left"),sQuery(id+"F10.wireOp",EDGE,"E179.right"),sQuery(id+"F10.wireOp",EDGE,"E180.MirrorCS"),sQuery(id+"F10.wireOp",EDGE,"E181.MirrorCS"),sQuery(id+"F10.wireOp",EDGE,"E182.MirrorCS"),sQuery(id+"F10.wireOp",EDGE,"E183.MirrorCS")])],"isStart":false});
            var sketch = newSketch(context, id + "F12", { "sketchPlane" : qUnion([Q0])});
            skCircle(sketch, "E207", {"center": v(-14, -23.5) * mm, "radius": 0.5 * mm});
            skCircle(sketch, "E208", {"center": v(-15.6, -23.5) * mm, "radius": 0.5 * mm});
            skCircle(sketch, "E209", {"center": v(-15.6, -27.5) * mm, "radius": 0.5 * mm});
            skCircle(sketch, "E210", {"center": v(-14, -27.5) * mm, "radius": 0.5 * mm});
            skCircle(sketch, "E211.MirrorC", {"center": v(14, -27.5) * mm, "radius": 0.5 * mm});
            skCircle(sketch, "E212.MirrorC", {"center": v(15.6, -27.5) * mm, "radius": 0.5 * mm});
            skCircle(sketch, "E213.MirrorC", {"center": v(15.6, -23.5) * mm, "radius": 0.5 * mm});
            skCircle(sketch, "E214.MirrorC", {"center": v(14, -23.5) * mm, "radius": 0.5 * mm});
            skSolve(sketch);
        }
        {
            var Q0;
            Q0=qSketchRegion(id+"F12",true);
            extrude(context, id + "F13", {"entities" : qUnion([Q0]), "operationType" : NewBodyOperationType.REMOVE, "oppositeDirection" : true, "depth" : 25 * mm});
        }
        {
            var Q0;
            Q0=qCreatedBy(makeId("Top.planeOp"),FACE);
            var sketch = newSketch(context, id + "F14", { "sketchPlane" : qUnion([Q0])});
            skCircle(sketch, "E215", {"center": v(0, 0) * mm, "radius": 3.15 * mm});
            skCircle(sketch, "E216", {"center": v(0, 0) * mm, "radius": 1.25 * mm});
            skSolve(sketch);
        }
        {
            var Q0;
            Q0=makeQuery(id+"F14.imprint","IMPRINT",FACE,{"disambiguationData":[TD([[makeQuery(id+"F14.imprint","IMPRINT",EDGE,{"derivedFrom":sQuery(id+"F14.wireOp",EDGE,"E215")}),1.0]])]});
            extrude(context, id + "F15", {"entities" : qUnion([Q0]), "depth" : 30 * mm});
        }
        {
            var Q0;
            Q0=makeQuery(id+"F7.opExtrude","SWEPT_EDGE",EDGE,{"disambiguationData":[OSD([sQuery(id+"F6.wireOp",EDGE,"E129"),sQuery(id+"F6.wireOp",EDGE,"E130")])]});
            fillet(context, id + "F16", {"entities" : qUnion([Q0]), "radius" : 1 * mm, "tangentPropagation" : true, "allowEdgeOverflow" : false});
        }
        {
            var Q0;
            Q0=qCreatedBy(makeId("Top.planeOp"),FACE);
            var sketch = newSketch(context, id + "F17", { "sketchPlane" : qUnion([Q0])});
            skCircle(sketch, "E217", {"center": v(0, 0) * mm, "radius": 2.23 * mm});
            skCircle(sketch, "E218", {"center": v(0, 0) * mm, "radius": 1.25 * mm});
            skSolve(sketch);
        }
        {
            var Q0;
            Q0=makeQuery(id+"F17.imprint","IMPRINT",FACE,{"disambiguationData":[TD([[makeQuery(id+"F17.imprint","IMPRINT",EDGE,{"derivedFrom":sQuery(id+"F17.wireOp",EDGE,"E217")}),1.0]])]});
            extrude(context, id + "F18", {"entities" : qUnion([Q0]), "depth" : 1.5 * mm});
        }
        {
            var Q0;
            Q0=makeQuery(id+"F18.opExtrude","CAP_FACE",FACE,{"disambiguationData":[OSD([sQuery(id+"F17.wireOp",EDGE,"E217"),sQuery(id+"F17.wireOp",EDGE,"E218")])],"isStart":false});
            var sketch = newSketch(context, id + "F19", { "sketchPlane" : qUnion([Q0])});
            skCircle(sketch, "E219", {"center": v(0, 0) * mm, "radius": 2.75 * mm});
            skCircle(sketch, "E220", {"center": v(0, 0) * mm, "radius": 1.25 * mm});
            skSolve(sketch);
        }
        {
            var Q0;
            Q0=qSketchRegion(id+"F19",true);
            extrude(context, id + "F20", {"entities" : qUnion([Q0]), "operationType" : NewBodyOperationType.ADD, "depth" : 1.5 * mm});
        }
        {
            var Q0;
            Q0=qCreatedBy(makeId("Right.planeOp"),FACE);
            var sketch = newSketch(context, id + "F21", { "sketchPlane" : qUnion([Q0])});
            skLineSegment(sketch, "E221.top", {"start": v(-30.4, -1.5) * mm, "end": v(-25.5, -1.5) * mm});
            skLineSegment(sketch, "E221.left", {"start": v(-30.4, 0) * mm, "end": v(-30.4, -1.5) * mm});
            skLineSegment(sketch, "E221.right", {"start": v(-25.5, 0) * mm, "end": v(-25.5, -1.5) * mm});
            skLineSegment(sketch, "E222.bottom", {"start": v(-27.9, 37) * mm, "end": v(-23, 37) * mm});
            skLineSegment(sketch, "E222.top", {"start": v(-27.9, 35.5) * mm, "end": v(-23, 35.5) * mm, "construction": true});
            skLineSegment(sketch, "E222.left", {"start": v(-27.9, 37) * mm, "end": v(-27.9, 35.5) * mm});
            skLineSegment(sketch, "E222.right", {"start": v(-23, 37) * mm, "end": v(-23, 35.5) * mm});
            skLineSegment(sketch, "E223", {"start": v(-23, 35.5) * mm, "end": v(-19, 35.5) * mm});
            skLineSegment(sketch, "E224", {"start": v(-27.9, 35.5) * mm, "end": v(-30.9, 35.5) * mm});
            skLineSegment(sketch, "E225", {"start": v(-25.5, 0) * mm, "end": v(-25.5, 6) * mm});
            skLineSegment(sketch, "E226", {"start": v(-25.5, 6) * mm, "end": v(-19, 6) * mm});
            skPoint(sketch, "E227.visualSharp", {"position": v(-25.5, 6) * mm});
            skLineSegment(sketch, "E228", {"start": v(-30.4, 0) * mm, "end": v(-35.4, 0) * mm});
            skLineSegment(sketch, "E229", {"start": v(-19, 35.5) * mm, "end": v(-19, 6) * mm});
            skArc(sketch, "E230", {"start": v(-30.9, 35.5) * mm, "mid": v(-35.86, 18.1) * mm, "end": v(-35.4, 0) * mm});
            skCircle(sketch, "E231", {"center": v(-33.5, 11.5) * mm, "radius": 1.55 * mm});
            skLineSegment(sketch, "E232", {"start": v(-40.89, 0.08) * mm, "end": v(-20.97, 16.8) * mm, "construction": true});
            skLineSegment(sketch, "E233", {"start": v(-33.5, 11.5) * mm, "end": v(-30.93, 8.44) * mm, "construction": true});
            skCircle(sketch, "E234", {"center": v(-31.6, 12.7) * mm, "radius": 1.55 * mm});
            skLineSegment(sketch, "E235", {"start": v(-31.6, 12.7) * mm, "end": v(-29.3, 10.77) * mm, "construction": true});
            skLineSegment(sketch, "E236", {"start": v(-37.66, 0.81) * mm, "end": v(-20.95, 20.73) * mm, "construction": true});
            skCircle(sketch, "E237", {"center": v(-29.6, 14.2) * mm, "radius": 1.55 * mm});
            skLineSegment(sketch, "E238", {"start": v(-33.5, 1.44) * mm, "end": v(-20.5, 23.96) * mm, "construction": true});
            skLineSegment(sketch, "E239", {"start": v(-29.6, 14.2) * mm, "end": v(-27, 12.7) * mm, "construction": true});
            skCircle(sketch, "E240", {"center": v(-27.9, 15.5) * mm, "radius": 1.55 * mm});
            skLineSegment(sketch, "E241", {"start": v(-27.9, 15.5) * mm, "end": v(-25.08, 14.47) * mm, "construction": true});
            skLineSegment(sketch, "E242", {"start": v(-29.53, 2.26) * mm, "end": v(-20.63, 26.69) * mm, "construction": true});
            skSolve(sketch);
        }
        {
            var Q0;
            Q0=makeQuery(id+"F21.imprint","IMPRINT",FACE,{"disambiguationData":[TD([[makeQuery(id+"F21.imprint","IMPRINT",EDGE,{"derivedFrom":sQuery(id+"F21.wireOp",EDGE,"E221.top")}),1.0]])]});
            extrude(context, id + "F22", {"entities" : qUnion([Q0]), "depth" : 1.5 * mm});
        }
        {
            var Q0;
            Q0=makeQuery(id+"F22.opExtrude","CAP_FACE",FACE,{"disambiguationData":[OSD([sQuery(id+"F21.wireOp",EDGE,"E221.top"),sQuery(id+"F21.wireOp",EDGE,"E221.left"),sQuery(id+"F21.wireOp",EDGE,"E221.right"),sQuery(id+"F21.wireOp",EDGE,"E222.bottom"),sQuery(id+"F21.wireOp",EDGE,"E222.left"),sQuery(id+"F21.wireOp",EDGE,"E222.right"),sQuery(id+"F21.wireOp",EDGE,"E223"),sQuery(id+"F21.wireOp",EDGE,"E224"),sQuery(id+"F21.wireOp",EDGE,"E225"),sQuery(id+"F21.wireOp",EDGE,"E226"),sQuery(id+"F21.wireOp",EDGE,"E228"),sQuery(id+"F21.wireOp",EDGE,"E229"),sQuery(id+"F21.wireOp",EDGE,"E230"),sQuery(id+"F21.wireOp",EDGE,"IlX3JSMu-NUec-YmUJ-kGKA-v2RqxQZpXFZG"),sQuery(id+"F21.wireOp",EDGE,"QqSHGALd-vgMH-CsCO-2UtY-GNjF0gbNKMfq"),sQuery(id+"F21.wireOp",EDGE,"c9571d5d-53fe-49e0-8d75-11ff31d18f6d.1.0.0"),sQuery(id+"F21.wireOp",EDGE,"c9571d5d-53fe-49e0-8d75-11ff31d18f6d.2.0.0"),sQuery(id+"F21.wireOp",EDGE,"125c3161-0d2e-4c84-b0d3-5869db5af3f9.trimOffspring"),sQuery(id+"F21.wireOp",EDGE,"ea2af63f-a69e-4b98-8f0a-1ea5ec80e0f0.1.0.0"),sQuery(id+"F21.wireOp",EDGE,"8b0a454f-8ec5-4ccb-b880-c8bcff42a064.trimOffspring"),sQuery(id+"F21.wireOp",EDGE,"b1a4fc6e-4469-44ba-9b3a-8baa4c264c5c.trimOffspring"),sQuery(id+"F21.wireOp",EDGE,"E231"),sQuery(id+"F21.wireOp",EDGE,"baf5fba7-d95c-4aec-8581-47ca1ced992e.0.3.0"),sQuery(id+"F21.wireOp",EDGE,"baf5fba7-d95c-4aec-8581-47ca1ced992e.0.4.0"),sQuery(id+"F21.wireOp",EDGE,"f055a136-d7f1-46da-b909-f311c71264d7.trimOffspring"),sQuery(id+"F21.wireOp",EDGE,"9be788b4-47e9-4e63-ba09-159407b564ad.trimOffspring"),sQuery(id+"F21.wireOp",EDGE,"186d221a-cc9f-4302-9d80-a85e1b2c8977.trimOffspring"),sQuery(id+"F21.wireOp",EDGE,"oNhZRw74-Onx2-UYVr-j9Fp-hqOf6hEBPdf1")])],"isStart":false});
            var sketch = newSketch(context, id + "F23", { "sketchPlane" : qUnion([Q0])});
            skLineSegment(sketch, "E243.bottom", {"start": v(-19, 6) * mm, "end": v(-22.5, 6) * mm});
            skLineSegment(sketch, "E243.top", {"start": v(-19, 14) * mm, "end": v(-20.5, 14) * mm});
            skLineSegment(sketch, "E243.left", {"start": v(-19, 6) * mm, "end": v(-19, 14) * mm});
            skLineSegment(sketch, "E243.right", {"start": v(-22.5, 6) * mm, "end": v(-22.5, 12) * mm});
            skPoint(sketch, "E244.visualSharp", {"position": v(-22.5, 14) * mm});
            skArc(sketch, "E244.filletArc", {"start": v(-20.5, 14) * mm, "mid": v(-21.91, 13.41) * mm, "end": v(-22.5, 12) * mm});
            skArc(sketch, "E245", {"start": v(-26.57, 27.48) * mm, "mid": v(-29.06, 26.8) * mm, "end": v(-28.14, 24.37) * mm});
            skArc(sketch, "E246", {"start": v(-22.86, 24.37) * mm, "mid": v(-21.94, 26.8) * mm, "end": v(-24.43, 27.48) * mm});
            skArc(sketch, "E247", {"start": v(-26.95, 23.04) * mm, "mid": v(-25.5, 21.94) * mm, "end": v(-24.05, 23.04) * mm});
            skArc(sketch, "E248", {"start": v(-26.57, 27.48) * mm, "mid": v(-25.5, 27.17) * mm, "end": v(-24.43, 27.48) * mm});
            skArc(sketch, "E249", {"start": v(-26.95, 23.04) * mm, "mid": v(-27.39, 23.85) * mm, "end": v(-28.14, 24.37) * mm});
            skArc(sketch, "E250", {"start": v(-22.86, 24.37) * mm, "mid": v(-23.61, 23.85) * mm, "end": v(-24.05, 23.04) * mm});
            skLineSegment(sketch, "E251", {"start": v(-27.5, 26) * mm, "end": v(-23.5, 26) * mm, "construction": true});
            skLineSegment(sketch, "E252", {"start": v(-25.5, 23.44) * mm, "end": v(-25.5, 26) * mm, "construction": true});
            skSolve(sketch);
        }
        {
            var Q0;
            Q0=qSketchRegion(id+"F23",true);
            extrude(context, id + "F24", {"entities" : qUnion([Q0]), "operationType" : NewBodyOperationType.REMOVE, "oppositeDirection" : true, "depth" : 25 * mm});
        }
        {
            var Q0;
            Q0=makeQuery(id+"F22.opExtrude","CAP_FACE",FACE,{"disambiguationData":[OSD([sQuery(id+"F21.wireOp",EDGE,"E221.top"),sQuery(id+"F21.wireOp",EDGE,"E221.left"),sQuery(id+"F21.wireOp",EDGE,"E221.right"),sQuery(id+"F21.wireOp",EDGE,"E222.bottom"),sQuery(id+"F21.wireOp",EDGE,"E222.left"),sQuery(id+"F21.wireOp",EDGE,"E222.right"),sQuery(id+"F21.wireOp",EDGE,"E223"),sQuery(id+"F21.wireOp",EDGE,"E224"),sQuery(id+"F21.wireOp",EDGE,"E225"),sQuery(id+"F21.wireOp",EDGE,"E226"),sQuery(id+"F21.wireOp",EDGE,"E228"),sQuery(id+"F21.wireOp",EDGE,"E229"),sQuery(id+"F21.wireOp",EDGE,"E230"),sQuery(id+"F21.wireOp",EDGE,"IlX3JSMu-NUec-YmUJ-kGKA-v2RqxQZpXFZG"),sQuery(id+"F21.wireOp",EDGE,"QqSHGALd-vgMH-CsCO-2UtY-GNjF0gbNKMfq"),sQuery(id+"F21.wireOp",EDGE,"c9571d5d-53fe-49e0-8d75-11ff31d18f6d.1.0.0"),sQuery(id+"F21.wireOp",EDGE,"c9571d5d-53fe-49e0-8d75-11ff31d18f6d.2.0.0"),sQuery(id+"F21.wireOp",EDGE,"125c3161-0d2e-4c84-b0d3-5869db5af3f9.trimOffspring"),sQuery(id+"F21.wireOp",EDGE,"ea2af63f-a69e-4b98-8f0a-1ea5ec80e0f0.1.0.0"),sQuery(id+"F21.wireOp",EDGE,"8b0a454f-8ec5-4ccb-b880-c8bcff42a064.trimOffspring"),sQuery(id+"F21.wireOp",EDGE,"b1a4fc6e-4469-44ba-9b3a-8baa4c264c5c.trimOffspring"),sQuery(id+"F21.wireOp",EDGE,"E231"),sQuery(id+"F21.wireOp",EDGE,"baf5fba7-d95c-4aec-8581-47ca1ced992e.0.3.0"),sQuery(id+"F21.wireOp",EDGE,"baf5fba7-d95c-4aec-8581-47ca1ced992e.0.4.0"),sQuery(id+"F21.wireOp",EDGE,"f055a136-d7f1-46da-b909-f311c71264d7.trimOffspring"),sQuery(id+"F21.wireOp",EDGE,"9be788b4-47e9-4e63-ba09-159407b564ad.trimOffspring"),sQuery(id+"F21.wireOp",EDGE,"186d221a-cc9f-4302-9d80-a85e1b2c8977.trimOffspring"),sQuery(id+"F21.wireOp",EDGE,"oNhZRw74-Onx2-UYVr-j9Fp-hqOf6hEBPdf1")])],"isStart":false});
            var sketch = newSketch(context, id + "F25", { "sketchPlane" : qUnion([Q0])});
            skCircle(sketch, "E253", {"center": v(-28.4, 35.5) * mm, "radius": 0.5 * mm});
            skCircle(sketch, "E254", {"center": v(-22.5, 35.5) * mm, "radius": 0.5 * mm});
            skCircle(sketch, "E255", {"center": v(-30.9, 0) * mm, "radius": 0.5 * mm});
            skCircle(sketch, "E256", {"center": v(-25, 6) * mm, "radius": 0.5 * mm});
            skSolve(sketch);
        }
        {
            var Q0;
            Q0=qSketchRegion(id+"F25",true);
            extrude(context, id + "F26", {"entities" : qUnion([Q0]), "operationType" : NewBodyOperationType.REMOVE, "oppositeDirection" : true, "depth" : 25 * mm});
        }
        {
            var Q0;
            Q0=qCreatedBy(makeId("Top.planeOp"),FACE);
            var sketch = newSketch(context, id + "F27", { "sketchPlane" : qUnion([Q0])});
            skCircle(sketch, "E257", {"center": v(25.5, -8.5) * mm, "radius": 6.25 * mm});
            skCircle(sketch, "E258", {"center": v(25.5, -8.5) * mm, "radius": 3.25 * mm});
            skSolve(sketch);
        }
        {
            var Q0;
            Q0=makeQuery(id+"F27.imprint","IMPRINT",FACE,{"disambiguationData":[TD([[makeQuery(id+"F27.imprint","IMPRINT",EDGE,{"derivedFrom":sQuery(id+"F27.wireOp",EDGE,"E257")}),1.0]])]});
            extrude(context, id + "F28", {"entities" : qUnion([Q0]), "operationType" : NewBodyOperationType.ADD, "depth" : 1.5 * mm, "offsetDistance" : 25 * mm});
        }
        {
            var Q0;
            Q0=makeQuery(id+"F22.opExtrude","CAP_FACE",FACE,{"disambiguationData":[OSD([sQuery(id+"F21.wireOp",EDGE,"E221.top"),sQuery(id+"F21.wireOp",EDGE,"E221.left"),sQuery(id+"F21.wireOp",EDGE,"E221.right"),sQuery(id+"F21.wireOp",EDGE,"E222.bottom"),sQuery(id+"F21.wireOp",EDGE,"E222.left"),sQuery(id+"F21.wireOp",EDGE,"E222.right"),sQuery(id+"F21.wireOp",EDGE,"E223"),sQuery(id+"F21.wireOp",EDGE,"E224"),sQuery(id+"F21.wireOp",EDGE,"E225"),sQuery(id+"F21.wireOp",EDGE,"E226"),sQuery(id+"F21.wireOp",EDGE,"E228"),sQuery(id+"F21.wireOp",EDGE,"E229"),sQuery(id+"F21.wireOp",EDGE,"E230"),sQuery(id+"F21.wireOp",EDGE,"E231"),sQuery(id+"F21.wireOp",EDGE,"E234"),sQuery(id+"F21.wireOp",EDGE,"E237"),sQuery(id+"F21.wireOp",EDGE,"E240")])],"isStart":false});
            var sketch = newSketch(context, id + "F29", { "sketchPlane" : qUnion([Q0])});
            skCircle(sketch, "E259", {"center": v(-24, 16) * mm, "radius": 1.55 * mm});
            skSolve(sketch);
        }
        {
            var Q0;
            Q0=qSketchRegion(id+"F29",true);
            extrude(context, id + "F30", {"entities" : qUnion([Q0]), "operationType" : NewBodyOperationType.REMOVE, "oppositeDirection" : true, "depth" : 25 * mm, "offsetDistance" : 25 * mm});
        }
        {
            var Q0;
            Q0=qCreatedBy(makeId("Top.planeOp"),FACE);
            var sketch = newSketch(context, id + "F31", { "sketchPlane" : qUnion([Q0])});
            skArc(sketch, "E260", {"start": v(27.1, -14.54) * mm, "mid": v(25.73, -15.78) * mm, "end": v(25.95, -17.6) * mm});
            skLineSegment(sketch, "E261", {"start": v(25.95, -17.6) * mm, "end": v(19.9, -12.54) * mm});
            skLineSegment(sketch, "E262", {"start": v(19.9, -12.54) * mm, "end": v(27.1, -12.54) * mm});
            skLineSegment(sketch, "E263", {"start": v(27.1, -12.54) * mm, "end": v(27.1, -14.54) * mm});
            skSolve(sketch);
        }
        {
            var Q0;
            Q0=qSketchRegion(id+"F31",true);
            extrude(context, id + "F32", {"entities" : qUnion([Q0]), "operationType" : NewBodyOperationType.ADD, "depth" : 1.5 * mm, "offsetDistance" : 25 * mm});
        }
        {
            var Q0;
            Q0=qCreatedBy(makeId("Right.planeOp"),FACE);
            var sketch = newSketch(context, id + "F33", { "sketchPlane" : qUnion([Q0])});
            skLineSegment(sketch, "E264.bottom", {"start": v(-4.25, 24) * mm, "end": v(-4.25, 24) * mm});
            skLineSegment(sketch, "E264.top", {"start": v(-4.25, 6) * mm, "end": v(-4.25, 6) * mm});
            skLineSegment(sketch, "E264.left", {"start": v(-4.25, 24) * mm, "end": v(-4.25, 6) * mm});
            skLineSegment(sketch, "E264.right", {"start": v(-2.25, 22) * mm, "end": v(-2.25, 8) * mm});
            skPoint(sketch, "E265.visualSharp", {"position": v(-2.25, 24) * mm});
            skArc(sketch, "E265.filletArc", {"start": v(-2.25, 22) * mm, "mid": v(-2.84, 23.41) * mm, "end": v(-4.25, 24) * mm});
            skPoint(sketch, "E266.visualSharp", {"position": v(-2.25, 6) * mm});
            skArc(sketch, "E266.filletArc", {"start": v(-4.25, 6) * mm, "mid": v(-2.84, 6.59) * mm, "end": v(-2.25, 8) * mm});
            skLineSegment(sketch, "E267", {"start": v(0, 0) * mm, "end": v(0, 39.06) * mm, "construction": true});
            skSolve(sketch);
        }
        {
            var Q0;
            Q0=qSketchRegion(id+"F33",true);
            var Q1;
            Q1=sQuery(id+"F33.wireOp",EDGE,"E267");
            revolve(context, id + "F34", {"operationType" : NewBodyOperationType.REMOVE, "entities" : qUnion([Q0]), "axis" : qUnion([Q1]), "revolveType" : RevolveType.FULL, "oppositeDirection" : true});
        }
        {
            var Q0;
            Q0=makeQuery(id+"F34.boolean.opBoolean","INTERSECT",EDGE,{"derivedFrom":[makeQuery(id+"F15.opExtrude","SWEPT_FACE",FACE,{"disambiguationData":[OSD([sQuery(id+"F14.wireOp",EDGE,"E215")])]}),makeQuery(id+"F34.opRevolve","SWEPT_FACE",FACE,{"disambiguationData":[OSD([sQuery(id+"F33.wireOp",EDGE,"E265.filletArc")])]})]});
            var Q1;
            Q1=makeQuery(id+"F34.boolean.opBoolean","INTERSECT",EDGE,{"derivedFrom":[makeQuery(id+"F15.opExtrude","SWEPT_FACE",FACE,{"disambiguationData":[OSD([sQuery(id+"F14.wireOp",EDGE,"E215")])]}),makeQuery(id+"F34.opRevolve","SWEPT_FACE",FACE,{"disambiguationData":[OSD([sQuery(id+"F33.wireOp",EDGE,"E266.filletArc")])]})]});
            fillet(context, id + "F35", {"entities" : qUnion([Q0, Q1]), "radius" : 2 * mm, "tangentPropagation" : true, "allowEdgeOverflow" : false});
        }
        {
            var Q0;
            Q0=makeQuery(id+"F3.opExtrude","SWEPT_EDGE",EDGE,{"disambiguationData":[OSD([sQuery(id+"F2.wireOp",EDGE,"E96"),sQuery(id+"F2.wireOp",EDGE,"E97")])]});
            var Q1;
            Q1=makeQuery(id+"F3.opExtrude","SWEPT_EDGE",EDGE,{"disambiguationData":[OSD([sQuery(id+"F2.wireOp",EDGE,"E98.MirrorCS"),sQuery(id+"F2.wireOp",EDGE,"E99.MirrorCS")])]});
            fillet(context, id + "F36", {"entities" : qUnion([Q0, Q1]), "radius" : 2 * mm, "tangentPropagation" : true, "allowEdgeOverflow" : false});
        }
        {
            var Q0;
            Q0=makeQuery(id+"F3.opExtrude","CAP_FACE",FACE,{"disambiguationData":[OSD([sQuery(id+"F2.wireOp",EDGE,"E57"),sQuery(id+"F2.wireOp",EDGE,"E58"),sQuery(id+"F2.wireOp",EDGE,"E59"),sQuery(id+"F2.wireOp",EDGE,"E60"),sQuery(id+"F2.wireOp",EDGE,"E61.filletArc"),sQuery(id+"F2.wireOp",EDGE,"7c283ec5-88dc-4330-9acd-45fa73696fd11.MirrorCS"),sQuery(id+"F2.wireOp",EDGE,"E63.MirrorCS"),sQuery(id+"F2.wireOp",EDGE,"E64.MirrorCS"),sQuery(id+"F2.wireOp",EDGE,"E65.MirrorC"),sQuery(id+"F2.wireOp",EDGE,"E66.MirrorC"),sQuery(id+"F2.wireOp",EDGE,"9822711c-84ae-4c2d-bbd4-b3a60979fe173.MirrorCS"),sQuery(id+"F2.wireOp",EDGE,"E69.MirrorCS"),sQuery(id+"F2.wireOp",EDGE,"4a2114cf-ddcc-4bd1-b273-f588f7a722dc0.MirrorCS"),sQuery(id+"F2.wireOp",EDGE,"E70.MirrorCS"),sQuery(id+"F2.wireOp",EDGE,"E72.MirrorC"),sQuery(id+"F2.wireOp",EDGE,"E73.MirrorC"),sQuery(id+"F2.wireOp",EDGE,"E74.MirrorCS"),sQuery(id+"F2.wireOp",EDGE,"E75.MirrorC"),sQuery(id+"F2.wireOp",EDGE,"E76.MirrorC"),sQuery(id+"F2.wireOp",EDGE,"E77.MirrorCS"),sQuery(id+"F2.wireOp",EDGE,"b8184357-9e1d-4d76-b8cc-bd6e0700e5e00.MirrorCS"),sQuery(id+"F2.wireOp",EDGE,"ed51ebd1-3bfc-4bb5-896a-a1a15a693a9f0.MirrorCS"),sQuery(id+"F2.wireOp",EDGE,"E78.bottom"),sQuery(id+"F2.wireOp",EDGE,"E78.top"),sQuery(id+"F2.wireOp",EDGE,"E78.left"),sQuery(id+"F2.wireOp",EDGE,"E78.right"),sQuery(id+"F2.wireOp",EDGE,"E79.MirrorCS"),sQuery(id+"F2.wireOp",EDGE,"E80.MirrorCS"),sQuery(id+"F2.wireOp",EDGE,"E81.MirrorCS"),sQuery(id+"F2.wireOp",EDGE,"E82.MirrorCS"),sQuery(id+"F2.wireOp",EDGE,"E85"),sQuery(id+"F2.wireOp",EDGE,"E86"),sQuery(id+"F2.wireOp",EDGE,"E87.MirrorCS"),sQuery(id+"F2.wireOp",EDGE,"E88.MirrorCS"),sQuery(id+"F2.wireOp",EDGE,"4c566042-07f8-4978-bd30-aa573336a23a.filletArc"),sQuery(id+"F2.wireOp",EDGE,"15f95f9f-3696-4d3a-9986-670236afa415.filletArc"),sQuery(id+"F2.wireOp",EDGE,"E89"),sQuery(id+"F2.wireOp",EDGE,"E91.MirrorCS"),sQuery(id+"F2.wireOp",EDGE,"E92.MirrorCS"),sQuery(id+"F2.wireOp",EDGE,"E93.MirrorCS"),sQuery(id+"F2.wireOp",EDGE,"E96"),sQuery(id+"F2.wireOp",EDGE,"E97"),sQuery(id+"F2.wireOp",EDGE,"E98.MirrorCS"),sQuery(id+"F2.wireOp",EDGE,"E99.MirrorCS"),sQuery(id+"F2.wireOp",EDGE,"bcf1264d-b733-40b0-8774-b1950e08d1530.MirrorCS"),sQuery(id+"F2.wireOp",EDGE,"9af283ad-2154-46af-ae04-832c548851d70.MirrorCS"),sQuery(id+"F2.wireOp",EDGE,"E100"),sQuery(id+"F2.wireOp",EDGE,"E101.MirrorCS"),sQuery(id+"F2.wireOp",EDGE,"E102.filletArc"),sQuery(id+"F2.wireOp",EDGE,"E103.filletArc"),sQuery(id+"F2.wireOp",EDGE,"vuY6w2it-mn66-yzEo-Y1Tz-2XmqXBiDKGcJ")])],"isStart":false});
            var sketch = newSketch(context, id + "F37", { "sketchPlane" : qUnion([Q0])});
            skLineSegment(sketch, "E268", {"start": v(-4.5, 34) * mm, "end": v(-4.5, 31) * mm, "construction": true});
            skArc(sketch, "E269.0.startCap", {"start": v(-6, 34) * mm, "mid": v(-4.5, 35.5) * mm, "end": v(-3, 34) * mm});
            skArc(sketch, "E269.0.endCap", {"start": v(-3, 31) * mm, "mid": v(-4.5, 29.5) * mm, "end": v(-6, 31) * mm});
            skLineSegment(sketch, "E269.0.left", {"start": v(-3, 34) * mm, "end": v(-3, 31) * mm});
            skLineSegment(sketch, "E269.0.right", {"start": v(-6, 34) * mm, "end": v(-6, 31) * mm});
            skArc(sketch, "E270.MirrorCS", {"start": v(3, 31) * mm, "mid": v(4.5, 29.5) * mm, "end": v(6, 31) * mm});
            skLineSegment(sketch, "E271.MirrorCS", {"start": v(4.5, 34) * mm, "end": v(4.5, 31) * mm, "construction": true});
            skLineSegment(sketch, "E272.MirrorCS", {"start": v(3, 34) * mm, "end": v(3, 31) * mm});
            skArc(sketch, "E273.MirrorCS", {"start": v(6, 34) * mm, "mid": v(4.5, 35.5) * mm, "end": v(3, 34) * mm});
            skLineSegment(sketch, "E274.MirrorCS", {"start": v(6, 34) * mm, "end": v(6, 31) * mm});
            skSolve(sketch);
        }
        {
            var Q0;
            Q0=qSketchRegion(id+"F37",true);
            extrude(context, id + "F38", {"entities" : qUnion([Q0]), "operationType" : NewBodyOperationType.REMOVE, "oppositeDirection" : true, "depth" : 25 * mm});
        }
        {
            var Q0;
            Q0=makeQuery(id+"F22.opExtrude","SWEPT_EDGE",EDGE,{"disambiguationData":[OSD([sQuery(id+"F21.wireOp",EDGE,"E228"),sQuery(id+"F21.wireOp",EDGE,"E230")])]});
            chamfer(context, id + "F39", {"entities" : qUnion([Q0]), "width" : 2 * mm, "tangentPropagation" : true});
        }
        {
            var Q0;
            Q0=makeQuery(id+"F11.opExtrude","CAP_FACE",FACE,{"disambiguationData":[OSD([sQuery(id+"F10.wireOp",EDGE,"E157"),sQuery(id+"F10.wireOp",EDGE,"E158"),sQuery(id+"F10.wireOp",EDGE,"E160"),sQuery(id+"F10.wireOp",EDGE,"E161.filletArc"),sQuery(id+"F10.wireOp",EDGE,"E163.MirrorCS"),sQuery(id+"F10.wireOp",EDGE,"E165.MirrorCS"),sQuery(id+"F10.wireOp",EDGE,"E166.MirrorC"),sQuery(id+"F10.wireOp",EDGE,"E168.MirrorCS"),sQuery(id+"F10.wireOp",EDGE,"E170.MirrorCS"),sQuery(id+"F10.wireOp",EDGE,"E171.MirrorCS"),sQuery(id+"F10.wireOp",EDGE,"E172.MirrorCS"),sQuery(id+"F10.wireOp",EDGE,"E173.MirrorCS"),sQuery(id+"F10.wireOp",EDGE,"E174.MirrorCS"),sQuery(id+"F10.wireOp",EDGE,"E175.MirrorCS"),sQuery(id+"F10.wireOp",EDGE,"E176.MirrorCS"),sQuery(id+"F10.wireOp",EDGE,"E177.MirrorC"),sQuery(id+"F10.wireOp",EDGE,"E178.MirrorC"),sQuery(id+"F10.wireOp",EDGE,"E179.bottom"),sQuery(id+"F10.wireOp",EDGE,"E179.top"),sQuery(id+"F10.wireOp",EDGE,"E179.left"),sQuery(id+"F10.wireOp",EDGE,"E179.right"),sQuery(id+"F10.wireOp",EDGE,"E180.MirrorCS"),sQuery(id+"F10.wireOp",EDGE,"E181.MirrorCS"),sQuery(id+"F10.wireOp",EDGE,"E182.MirrorCS"),sQuery(id+"F10.wireOp",EDGE,"E183.MirrorCS"),sQuery(id+"F10.wireOp",EDGE,"E186"),sQuery(id+"F10.wireOp",EDGE,"E187"),sQuery(id+"F10.wireOp",EDGE,"E188.MirrorCS"),sQuery(id+"F10.wireOp",EDGE,"E189"),sQuery(id+"F10.wireOp",EDGE,"E190.trimOffspring"),sQuery(id+"F10.wireOp",EDGE,"E192.0.startCap"),sQuery(id+"F10.wireOp",EDGE,"E192.0.endCap"),sQuery(id+"F10.wireOp",EDGE,"E192.0.left"),sQuery(id+"F10.wireOp",EDGE,"E192.0.right"),sQuery(id+"F10.wireOp",EDGE,"E193.MirrorCS"),sQuery(id+"F10.wireOp",EDGE,"E194.MirrorCS"),sQuery(id+"F10.wireOp",EDGE,"E195.MirrorCS"),sQuery(id+"F10.wireOp",EDGE,"E196.MirrorCS"),sQuery(id+"F10.wireOp",EDGE,"E198"),sQuery(id+"F10.wireOp",EDGE,"E199"),sQuery(id+"F10.wireOp",EDGE,"E200"),sQuery(id+"F10.wireOp",EDGE,"E201"),sQuery(id+"F10.wireOp",EDGE,"E202.MirrorCS"),sQuery(id+"F10.wireOp",EDGE,"E203")])],"isStart":false});
            var sketch = newSketch(context, id + "F40", { "sketchPlane" : qUnion([Q0])});
            skLineSegment(sketch, "E275", {"start": v(-14, 15.75) * mm, "end": v(-14, 2.75) * mm, "construction": true});
            skArc(sketch, "E276.0.startCap", {"start": v(-15.25, 15.75) * mm, "mid": v(-14, 17) * mm, "end": v(-12.75, 15.75) * mm});
            skArc(sketch, "E276.0.endCap", {"start": v(-12.75, 2.75) * mm, "mid": v(-14, 1.5) * mm, "end": v(-15.25, 2.75) * mm});
            skLineSegment(sketch, "E276.0.left", {"start": v(-12.75, 15.75) * mm, "end": v(-12.75, 2.75) * mm});
            skLineSegment(sketch, "E276.0.right", {"start": v(-15.25, 15.75) * mm, "end": v(-15.25, 2.75) * mm});
            skLineSegment(sketch, "E277.MirrorCS", {"start": v(-14, -15.75) * mm, "end": v(-14, -2.75) * mm, "construction": true});
            skLineSegment(sketch, "E278.MirrorCS", {"start": v(-12.75, -15.75) * mm, "end": v(-12.75, -2.75) * mm});
            skLineSegment(sketch, "E279.MirrorCS", {"start": v(-15.25, -15.75) * mm, "end": v(-15.25, -2.75) * mm});
            skArc(sketch, "E280.MirrorCS", {"start": v(-15.25, -15.75) * mm, "mid": v(-14, -17) * mm, "end": v(-12.75, -15.75) * mm});
            skArc(sketch, "E281.MirrorCS", {"start": v(-12.75, -2.75) * mm, "mid": v(-14, -1.5) * mm, "end": v(-15.25, -2.75) * mm});
            skLineSegment(sketch, "E282.MirrorCS", {"start": v(12.75, 15.75) * mm, "end": v(12.75, 2.75) * mm});
            skLineSegment(sketch, "E283.MirrorCS", {"start": v(15.25, -15.75) * mm, "end": v(15.25, -2.75) * mm});
            skArc(sketch, "E284.MirrorCS", {"start": v(12.75, 2.75) * mm, "mid": v(14, 1.5) * mm, "end": v(15.25, 2.75) * mm});
            skArc(sketch, "E285.MirrorCS", {"start": v(12.75, -2.75) * mm, "mid": v(14, -1.5) * mm, "end": v(15.25, -2.75) * mm});
            skLineSegment(sketch, "E286.MirrorCS", {"start": v(12.75, -15.75) * mm, "end": v(12.75, -2.75) * mm});
            skArc(sketch, "E287.MirrorCS", {"start": v(15.25, 15.75) * mm, "mid": v(14, 17) * mm, "end": v(12.75, 15.75) * mm});
            skLineSegment(sketch, "E288.MirrorCS", {"start": v(14, 15.75) * mm, "end": v(14, 2.75) * mm, "construction": true});
            skLineSegment(sketch, "E289.MirrorCS", {"start": v(15.25, 15.75) * mm, "end": v(15.25, 2.75) * mm});
            skLineSegment(sketch, "E290.MirrorCS", {"start": v(14, -15.75) * mm, "end": v(14, -2.75) * mm, "construction": true});
            skArc(sketch, "E291.MirrorCS", {"start": v(15.25, -15.75) * mm, "mid": v(14, -17) * mm, "end": v(12.75, -15.75) * mm});
            skLineSegment(sketch, "E292.bottom", {"start": v(-5, 2) * mm, "end": v(5, 2) * mm});
            skLineSegment(sketch, "E292.top", {"start": v(-5, -2) * mm, "end": v(5, -2) * mm});
            skLineSegment(sketch, "E292.left", {"start": v(-7, 0) * mm, "end": v(-7, 0) * mm});
            skLineSegment(sketch, "E292.right", {"start": v(7, 0) * mm, "end": v(7, 0) * mm});
            skPoint(sketch, "E292.middle", {"position": v(0, 0) * mm});
            skLineSegment(sketch, "E293.bottom", {"start": v(-5, 20) * mm, "end": v(5, 20) * mm});
            skLineSegment(sketch, "E293.top", {"start": v(-5, 6) * mm, "end": v(5, 6) * mm});
            skLineSegment(sketch, "E293.left", {"start": v(-7, 18) * mm, "end": v(-7, 8) * mm});
            skLineSegment(sketch, "E293.right", {"start": v(7, 18) * mm, "end": v(7, 8) * mm});
            skPoint(sketch, "E293.middle", {"position": v(0, 13) * mm});
            skPoint(sketch, "E294.visualSharp", {"position": v(-7, 20) * mm});
            skArc(sketch, "E294.filletArc", {"start": v(-5, 20) * mm, "mid": v(-6.41, 19.41) * mm, "end": v(-7, 18) * mm});
            skPoint(sketch, "E295.visualSharp", {"position": v(7, 20) * mm});
            skArc(sketch, "E295.filletArc", {"start": v(7, 18) * mm, "mid": v(6.41, 19.41) * mm, "end": v(5, 20) * mm});
            skPoint(sketch, "E296.visualSharp", {"position": v(7, 6) * mm});
            skArc(sketch, "E296.filletArc", {"start": v(5, 6) * mm, "mid": v(6.41, 6.59) * mm, "end": v(7, 8) * mm});
            skPoint(sketch, "E297.visualSharp", {"position": v(-7, 6) * mm});
            skArc(sketch, "E297.filletArc", {"start": v(-7, 8) * mm, "mid": v(-6.41, 6.59) * mm, "end": v(-5, 6) * mm});
            skPoint(sketch, "E298.visualSharp", {"position": v(-7, 2) * mm});
            skArc(sketch, "E298.filletArc", {"start": v(-5, 2) * mm, "mid": v(-6.41, 1.41) * mm, "end": v(-7, 0) * mm});
            skPoint(sketch, "E299.visualSharp", {"position": v(7, 2) * mm});
            skArc(sketch, "E299.filletArc", {"start": v(7, 0) * mm, "mid": v(6.41, 1.41) * mm, "end": v(5, 2) * mm});
            skPoint(sketch, "E300.visualSharp", {"position": v(7, -2) * mm});
            skArc(sketch, "E300.filletArc", {"start": v(5, -2) * mm, "mid": v(6.41, -1.41) * mm, "end": v(7, 0) * mm});
            skPoint(sketch, "E301.visualSharp", {"position": v(-7, -2) * mm});
            skArc(sketch, "E301.filletArc", {"start": v(-7, 0) * mm, "mid": v(-6.41, -1.41) * mm, "end": v(-5, -2) * mm});
            skArc(sketch, "E302.MirrorCS", {"start": v(-5, -20) * mm, "mid": v(-6.41, -19.41) * mm, "end": v(-7, -18) * mm});
            skArc(sketch, "E303.MirrorCS", {"start": v(5, -6) * mm, "mid": v(6.41, -6.59) * mm, "end": v(7, -8) * mm});
            skArc(sketch, "E304.MirrorCS", {"start": v(7, -18) * mm, "mid": v(6.41, -19.41) * mm, "end": v(5, -20) * mm});
            skArc(sketch, "E305.MirrorCS", {"start": v(-7, -8) * mm, "mid": v(-6.41, -6.59) * mm, "end": v(-5, -6) * mm});
            skPoint(sketch, "E306.MirrorP", {"position": v(7, -20) * mm});
            skLineSegment(sketch, "E307.MirrorCS", {"start": v(-5, -20) * mm, "end": v(5, -20) * mm});
            skLineSegment(sketch, "E308.MirrorCS", {"start": v(-7, -18) * mm, "end": v(-7, -8) * mm});
            skPoint(sketch, "E309.MirrorP", {"position": v(0, -13) * mm});
            skPoint(sketch, "E310.MirrorP", {"position": v(-7, -6) * mm});
            skLineSegment(sketch, "E311.MirrorCS", {"start": v(7, -18) * mm, "end": v(7, -8) * mm});
            skPoint(sketch, "E312.MirrorP", {"position": v(-7, -20) * mm});
            skPoint(sketch, "E313.MirrorP", {"position": v(7, -6) * mm});
            skLineSegment(sketch, "E314.MirrorCS", {"start": v(-5, -6) * mm, "end": v(5, -6) * mm});
            skLineSegment(sketch, "E315.bottom", {"start": v(-5, -24) * mm, "end": v(5, -24) * mm});
            skLineSegment(sketch, "E315.top", {"start": v(-5, -28) * mm, "end": v(5, -28) * mm});
            skLineSegment(sketch, "E315.left", {"start": v(-7, -26) * mm, "end": v(-7, -26) * mm});
            skLineSegment(sketch, "E315.right", {"start": v(7, -26) * mm, "end": v(7, -26) * mm});
            skPoint(sketch, "E315.middle", {"position": v(0, -26) * mm});
            skPoint(sketch, "E316.visualSharp", {"position": v(-7, -28) * mm});
            skArc(sketch, "E316.filletArc", {"start": v(-7, -26) * mm, "mid": v(-6.41, -27.41) * mm, "end": v(-5, -28) * mm});
            skPoint(sketch, "E317.visualSharp", {"position": v(-7, -24) * mm});
            skArc(sketch, "E317.filletArc", {"start": v(-5, -24) * mm, "mid": v(-6.41, -24.59) * mm, "end": v(-7, -26) * mm});
            skPoint(sketch, "E318.visualSharp", {"position": v(7, -28) * mm});
            skArc(sketch, "E318.filletArc", {"start": v(5, -28) * mm, "mid": v(6.41, -27.41) * mm, "end": v(7, -26) * mm});
            skPoint(sketch, "E319.visualSharp", {"position": v(7, -24) * mm});
            skArc(sketch, "E319.filletArc", {"start": v(7, -26) * mm, "mid": v(6.41, -24.59) * mm, "end": v(5, -24) * mm});
            skSolve(sketch);
        }
        {
            var Q0;
            Q0=qSketchRegion(id+"F40",true);
            extrude(context, id + "F41", {"entities" : qUnion([Q0]), "operationType" : NewBodyOperationType.REMOVE, "oppositeDirection" : true, "depth" : 25 * mm});
        }
        {
            var Q0;
            Q0=makeQuery(id+"F3.opExtrude","CAP_FACE",FACE,{"disambiguationData":[OSD([sQuery(id+"F2.wireOp",EDGE,"E57"),sQuery(id+"F2.wireOp",EDGE,"E58"),sQuery(id+"F2.wireOp",EDGE,"E59"),sQuery(id+"F2.wireOp",EDGE,"E60"),sQuery(id+"F2.wireOp",EDGE,"E61.filletArc"),sQuery(id+"F2.wireOp",EDGE,"7c283ec5-88dc-4330-9acd-45fa73696fd11.MirrorCS"),sQuery(id+"F2.wireOp",EDGE,"E63.MirrorCS"),sQuery(id+"F2.wireOp",EDGE,"E64.MirrorCS"),sQuery(id+"F2.wireOp",EDGE,"E65.MirrorC"),sQuery(id+"F2.wireOp",EDGE,"E66.MirrorC"),sQuery(id+"F2.wireOp",EDGE,"9822711c-84ae-4c2d-bbd4-b3a60979fe173.MirrorCS"),sQuery(id+"F2.wireOp",EDGE,"E69.MirrorCS"),sQuery(id+"F2.wireOp",EDGE,"4a2114cf-ddcc-4bd1-b273-f588f7a722dc0.MirrorCS"),sQuery(id+"F2.wireOp",EDGE,"E70.MirrorCS"),sQuery(id+"F2.wireOp",EDGE,"E72.MirrorC"),sQuery(id+"F2.wireOp",EDGE,"E73.MirrorC"),sQuery(id+"F2.wireOp",EDGE,"E74.MirrorCS"),sQuery(id+"F2.wireOp",EDGE,"E75.MirrorC"),sQuery(id+"F2.wireOp",EDGE,"E76.MirrorC"),sQuery(id+"F2.wireOp",EDGE,"E77.MirrorCS"),sQuery(id+"F2.wireOp",EDGE,"b8184357-9e1d-4d76-b8cc-bd6e0700e5e00.MirrorCS"),sQuery(id+"F2.wireOp",EDGE,"ed51ebd1-3bfc-4bb5-896a-a1a15a693a9f0.MirrorCS"),sQuery(id+"F2.wireOp",EDGE,"E78.bottom"),sQuery(id+"F2.wireOp",EDGE,"E78.top"),sQuery(id+"F2.wireOp",EDGE,"E78.left"),sQuery(id+"F2.wireOp",EDGE,"E78.right"),sQuery(id+"F2.wireOp",EDGE,"E79.MirrorCS"),sQuery(id+"F2.wireOp",EDGE,"E80.MirrorCS"),sQuery(id+"F2.wireOp",EDGE,"E81.MirrorCS"),sQuery(id+"F2.wireOp",EDGE,"E82.MirrorCS"),sQuery(id+"F2.wireOp",EDGE,"E85"),sQuery(id+"F2.wireOp",EDGE,"E86"),sQuery(id+"F2.wireOp",EDGE,"E87.MirrorCS"),sQuery(id+"F2.wireOp",EDGE,"E88.MirrorCS"),sQuery(id+"F2.wireOp",EDGE,"4c566042-07f8-4978-bd30-aa573336a23a.filletArc"),sQuery(id+"F2.wireOp",EDGE,"15f95f9f-3696-4d3a-9986-670236afa415.filletArc"),sQuery(id+"F2.wireOp",EDGE,"E89"),sQuery(id+"F2.wireOp",EDGE,"E91.MirrorCS"),sQuery(id+"F2.wireOp",EDGE,"E92.MirrorCS"),sQuery(id+"F2.wireOp",EDGE,"E93.MirrorCS"),sQuery(id+"F2.wireOp",EDGE,"E96"),sQuery(id+"F2.wireOp",EDGE,"E97"),sQuery(id+"F2.wireOp",EDGE,"E98.MirrorCS"),sQuery(id+"F2.wireOp",EDGE,"E99.MirrorCS"),sQuery(id+"F2.wireOp",EDGE,"E100"),sQuery(id+"F2.wireOp",EDGE,"E101.MirrorCS"),sQuery(id+"F2.wireOp",EDGE,"E102.filletArc"),sQuery(id+"F2.wireOp",EDGE,"E103.filletArc"),sQuery(id+"F2.wireOp",EDGE,"E104"),sQuery(id+"F2.wireOp",EDGE,"E107.filletArc"),sQuery(id+"F2.wireOp",EDGE,"E108.filletArc")])],"isStart":false});
            var sketch = newSketch(context, id + "F42", { "sketchPlane" : qUnion([Q0])});
            skArc(sketch, "E320", {"start": v(-1.84, -41.02) * mm, "mid": v(-3.61, -37.2) * mm, "end": v(-5.6, -33.5) * mm});
            skArc(sketch, "E321.MirrorC", {"start": v(1.84, -41.02) * mm, "mid": v(3.61, -37.2) * mm, "end": v(5.6, -33.5) * mm});
            skLineSegment(sketch, "E322", {"start": v(-4.73, -32) * mm, "end": v(4.73, -32) * mm});
            skPoint(sketch, "E323.visualSharp", {"position": v(0, -45.71) * mm});
            skArc(sketch, "E323.filletArc", {"start": v(-1.84, -41.02) * mm, "mid": v(0, -42.23) * mm, "end": v(1.84, -41.02) * mm});
            skPoint(sketch, "E324.visualSharp", {"position": v(-6.47, -32) * mm});
            skArc(sketch, "E324.filletArc", {"start": v(-4.73, -32) * mm, "mid": v(-5.6, -32.5) * mm, "end": v(-5.6, -33.5) * mm});
            skPoint(sketch, "E325.visualSharp", {"position": v(6.47, -32) * mm});
            skArc(sketch, "E325.filletArc", {"start": v(5.6, -33.5) * mm, "mid": v(5.6, -32.5) * mm, "end": v(4.73, -32) * mm});
            skSolve(sketch);
        }
        {
            var Q0;
            Q0=qSketchRegion(id+"F42",true);
            extrude(context, id + "F43", {"entities" : qUnion([Q0]), "operationType" : NewBodyOperationType.REMOVE, "oppositeDirection" : true, "depth" : 25 * mm});
        }
        {
            var Q0;
            Q0=makeQuery(id+"F28.boolean.opBoolean","INTERSECT",EDGE,{"derivedFrom":[makeQuery(id+"F1.opExtrude","SWEPT_FACE",FACE,{"disambiguationData":[OSD([sQuery(id+"F0.wireOp",EDGE,"E55.filletArc")])]}),makeQuery(id+"F28.opExtrude","SWEPT_FACE",FACE,{"disambiguationData":[OSD([sQuery(id+"F27.wireOp",EDGE,"E257")])]})]});
            fillet(context, id + "F44", {"entities" : qUnion([Q0]), "radius" : 2 * mm, "tangentPropagation" : true, "allowEdgeOverflow" : false});
        }
        {
            var Q0;
            Q0=makeQuery(id+"F22.opExtrude","CAP_FACE",FACE,{"disambiguationData":[OSD([sQuery(id+"F21.wireOp",EDGE,"E221.top"),sQuery(id+"F21.wireOp",EDGE,"E221.left"),sQuery(id+"F21.wireOp",EDGE,"E221.right"),sQuery(id+"F21.wireOp",EDGE,"E222.bottom"),sQuery(id+"F21.wireOp",EDGE,"E222.left"),sQuery(id+"F21.wireOp",EDGE,"E222.right"),sQuery(id+"F21.wireOp",EDGE,"E223"),sQuery(id+"F21.wireOp",EDGE,"E224"),sQuery(id+"F21.wireOp",EDGE,"E225"),sQuery(id+"F21.wireOp",EDGE,"E226"),sQuery(id+"F21.wireOp",EDGE,"E228"),sQuery(id+"F21.wireOp",EDGE,"E229"),sQuery(id+"F21.wireOp",EDGE,"E230"),sQuery(id+"F21.wireOp",EDGE,"E231"),sQuery(id+"F21.wireOp",EDGE,"E234"),sQuery(id+"F21.wireOp",EDGE,"E237"),sQuery(id+"F21.wireOp",EDGE,"E240")])],"isStart":false});
            var sketch = newSketch(context, id + "F45", { "sketchPlane" : qUnion([Q0])});
            skCircle(sketch, "E326", {"center": v(-23, 17) * mm, "radius": 1.55 * mm});
            skSolve(sketch);
        }
        {
            var Q0;
            Q0=makeQuery(id+"F45.imprint","IMPRINT",FACE,{"disambiguationData":[TD([[makeQuery(id+"F45.imprint","IMPRINT",EDGE,{"derivedFrom":sQuery(id+"F45.wireOp",EDGE,"E326")}),1.0]])]});
            extrude(context, id + "F46", {"entities" : qUnion([Q0]), "operationType" : NewBodyOperationType.REMOVE, "oppositeDirection" : true, "depth" : 25 * mm, "offsetDistance" : 25 * mm});
        }
        {
            var Q0;
            Q0=makeQuery(id+"F7.opExtrude","CAP_FACE",FACE,{"disambiguationData":[OSD([sQuery(id+"F6.wireOp",EDGE,"E125"),sQuery(id+"F6.wireOp",EDGE,"E126"),sQuery(id+"F6.wireOp",EDGE,"E128"),sQuery(id+"F6.wireOp",EDGE,"E129"),sQuery(id+"F6.wireOp",EDGE,"E130"),sQuery(id+"F6.wireOp",EDGE,"E131"),sQuery(id+"F6.wireOp",EDGE,"E132"),sQuery(id+"F6.wireOp",EDGE,"E133"),sQuery(id+"F6.wireOp",EDGE,"E138.trimOffspring"),sQuery(id+"F6.wireOp",EDGE,"E139.filletArc"),sQuery(id+"F6.wireOp",EDGE,"E140"),sQuery(id+"F6.wireOp",EDGE,"E141.trimOffspring"),sQuery(id+"F6.wireOp",EDGE,"E142.trimOffspring"),sQuery(id+"F6.wireOp",EDGE,"E143"),sQuery(id+"F6.wireOp",EDGE,"E144"),sQuery(id+"F6.wireOp",EDGE,"E145.trimOffspring"),sQuery(id+"F6.wireOp",EDGE,"E147.filletArc"),sQuery(id+"F6.wireOp",EDGE,"E148.filletArc"),sQuery(id+"F6.wireOp",EDGE,"E149.MirrorCS"),sQuery(id+"F6.wireOp",EDGE,"E150"),sQuery(id+"F6.wireOp",EDGE,"E151")])],"isStart":true});
            var sketch = newSketch(context, id + "F47", { "sketchPlane" : qUnion([Q0])});
            skLineSegment(sketch, "E327", {"start": v(-30, -10.25) * mm, "end": v(-16.25, -10.25) * mm});
            skLineSegment(sketch, "E328", {"start": v(-10.25, -16.25) * mm, "end": v(-10.25, -30) * mm});
            skLineSegment(sketch, "E329", {"start": v(-10.25, -30) * mm, "end": v(0, -30) * mm});
            skLineSegment(sketch, "E330", {"start": v(0, -30) * mm, "end": v(0, 0) * mm});
            skLineSegment(sketch, "E331", {"start": v(-30, -10.25) * mm, "end": v(-30, 0) * mm});
            skPoint(sketch, "E331.endSnap0", {"position": v(-3.33, 0) * mm});
            skLineSegment(sketch, "E332", {"start": v(-30, 0) * mm, "end": v(0, 0) * mm});
            skPoint(sketch, "E333.visualSharp", {"position": v(-10.25, -10.25) * mm});
            skArc(sketch, "E333.filletArc", {"start": v(-10.25, -16.25) * mm, "mid": v(-12, -12) * mm, "end": v(-16.25, -10.25) * mm});
            skSolve(sketch);
        }
        {
            var Q0;
            Q0 = qSketchRegion(id + "F47", true);
            extrude(context, id + "F48", {"entities" : qUnion([Q0]), "operationType" : NewBodyOperationType.REMOVE, "oppositeDirection" : true, "depth" : 2 * mm, "offsetDistance" : 25 * mm});
        }
        {
            var Q0;
            Q0=makeQuery(id+"F3.opExtrude","CAP_FACE",FACE,{"disambiguationData":[OSD([sQuery(id+"F2.wireOp",EDGE,"E57"),sQuery(id+"F2.wireOp",EDGE,"E58"),sQuery(id+"F2.wireOp",EDGE,"E59"),sQuery(id+"F2.wireOp",EDGE,"E60"),sQuery(id+"F2.wireOp",EDGE,"E63.MirrorCS"),sQuery(id+"F2.wireOp",EDGE,"E64.MirrorCS"),sQuery(id+"F2.wireOp",EDGE,"E65.MirrorC"),sQuery(id+"F2.wireOp",EDGE,"E66.MirrorC"),sQuery(id+"F2.wireOp",EDGE,"E69.MirrorCS"),sQuery(id+"F2.wireOp",EDGE,"E70.MirrorCS"),sQuery(id+"F2.wireOp",EDGE,"E72.MirrorC"),sQuery(id+"F2.wireOp",EDGE,"E73.MirrorC"),sQuery(id+"F2.wireOp",EDGE,"E74.MirrorCS"),sQuery(id+"F2.wireOp",EDGE,"E75.MirrorC"),sQuery(id+"F2.wireOp",EDGE,"E76.MirrorC"),sQuery(id+"F2.wireOp",EDGE,"E77.MirrorCS"),sQuery(id+"F2.wireOp",EDGE,"E78.bottom"),sQuery(id+"F2.wireOp",EDGE,"E78.top"),sQuery(id+"F2.wireOp",EDGE,"E78.left"),sQuery(id+"F2.wireOp",EDGE,"E78.right"),sQuery(id+"F2.wireOp",EDGE,"E79.MirrorCS"),sQuery(id+"F2.wireOp",EDGE,"E80.MirrorCS"),sQuery(id+"F2.wireOp",EDGE,"E81.MirrorCS"),sQuery(id+"F2.wireOp",EDGE,"E82.MirrorCS"),sQuery(id+"F2.wireOp",EDGE,"E85"),sQuery(id+"F2.wireOp",EDGE,"E86"),sQuery(id+"F2.wireOp",EDGE,"E87.MirrorCS"),sQuery(id+"F2.wireOp",EDGE,"E88.MirrorCS"),sQuery(id+"F2.wireOp",EDGE,"E89"),sQuery(id+"F2.wireOp",EDGE,"E91.MirrorCS"),sQuery(id+"F2.wireOp",EDGE,"E92.MirrorCS"),sQuery(id+"F2.wireOp",EDGE,"E93.MirrorCS"),sQuery(id+"F2.wireOp",EDGE,"E96"),sQuery(id+"F2.wireOp",EDGE,"E97"),sQuery(id+"F2.wireOp",EDGE,"E98.MirrorCS"),sQuery(id+"F2.wireOp",EDGE,"E99.MirrorCS"),sQuery(id+"F2.wireOp",EDGE,"E100"),sQuery(id+"F2.wireOp",EDGE,"E101.MirrorCS"),sQuery(id+"F2.wireOp",EDGE,"E102.filletArc"),sQuery(id+"F2.wireOp",EDGE,"E103.filletArc"),sQuery(id+"F2.wireOp",EDGE,"E104"),sQuery(id+"F2.wireOp",EDGE,"E107.filletArc"),sQuery(id+"F2.wireOp",EDGE,"E108.filletArc"),sQuery(id+"F2.wireOp",EDGE,"E109.filletArc"),sQuery(id+"F2.wireOp",EDGE,"E110.filletArc"),sQuery(id+"F2.wireOp",EDGE,"E111.filletArc"),sQuery(id+"F2.wireOp",EDGE,"E112.filletArc"),sQuery(id+"F2.wireOp",EDGE,"E113"),sQuery(id+"F2.wireOp",EDGE,"E114.filletArc"),sQuery(id+"F2.wireOp",EDGE,"E115.MirrorCS"),sQuery(id+"F2.wireOp",EDGE,"E116.filletArc")])],"isStart":false});
            var sketch = newSketch(context, id + "F49", { "sketchPlane" : qUnion([Q0])});
            skLineSegment(sketch, "E334.bottom", {"start": v(-6.34, 13) * mm, "end": v(6.34, 13) * mm});
            skLineSegment(sketch, "E334.top", {"start": v(-6.34, -13) * mm, "end": v(6.34, -13) * mm});
            skLineSegment(sketch, "E334.left", {"start": v(-13, 6.34) * mm, "end": v(-13, -6.34) * mm});
            skLineSegment(sketch, "E334.right", {"start": v(13, 6.34) * mm, "end": v(13, -6.34) * mm});
            skPoint(sketch, "E334.middle", {"position": v(0, 0) * mm});
            skLineSegment(sketch, "E335", {"start": v(13, 13) * mm, "end": v(-13, -13) * mm, "construction": true});
            skLineSegment(sketch, "E336", {"start": v(-13, 13) * mm, "end": v(13, -13) * mm, "construction": true});
            skLineSegment(sketch, "E337.0", {"start": v(-11.3, 7.05) * mm, "end": v(-4.95, 0.7) * mm});
            skLineSegment(sketch, "E338.0", {"start": v(-7.05, 11.3) * mm, "end": v(-0.7, 4.95) * mm});
            skLineSegment(sketch, "E339.0", {"start": v(11.3, 7.05) * mm, "end": v(4.95, 0.7) * mm});
            skLineSegment(sketch, "E340.0", {"start": v(7.05, 11.3) * mm, "end": v(0.7, 4.95) * mm});
            skLineSegment(sketch, "E341.trimOffspring", {"start": v(4.95, -0.7) * mm, "end": v(11.3, -7.05) * mm});
            skLineSegment(sketch, "E342.trimOffspring", {"start": v(-4.95, -0.7) * mm, "end": v(-11.3, -7.05) * mm});
            skLineSegment(sketch, "E343.trimOffspring", {"start": v(0.7, -4.95) * mm, "end": v(7.05, -11.3) * mm});
            skLineSegment(sketch, "E344.trimOffspring", {"start": v(-0.7, -4.95) * mm, "end": v(-7.05, -11.3) * mm});
            skPoint(sketch, "E345.visualSharp", {"position": v(-8.76, 13) * mm});
            skArc(sketch, "E345.filletArc", {"start": v(-6.34, 13) * mm, "mid": v(-7.27, 12.38) * mm, "end": v(-7.05, 11.3) * mm});
            skPoint(sketch, "E346.visualSharp", {"position": v(8.76, 13) * mm});
            skArc(sketch, "E346.filletArc", {"start": v(7.05, 11.3) * mm, "mid": v(7.27, 12.38) * mm, "end": v(6.34, 13) * mm});
            skPoint(sketch, "E347.visualSharp", {"position": v(0, 4.24) * mm});
            skArc(sketch, "E347.filletArc", {"start": v(-0.7, 4.95) * mm, "mid": v(0, 4.66) * mm, "end": v(0.7, 4.95) * mm});
            skPoint(sketch, "E348.visualSharp", {"position": v(13, 8.76) * mm});
            skArc(sketch, "E348.filletArc", {"start": v(13, 6.34) * mm, "mid": v(12.38, 7.27) * mm, "end": v(11.3, 7.05) * mm});
            skPoint(sketch, "E349.visualSharp", {"position": v(13, -8.76) * mm});
            skArc(sketch, "E349.filletArc", {"start": v(11.3, -7.05) * mm, "mid": v(12.38, -7.27) * mm, "end": v(13, -6.34) * mm});
            skPoint(sketch, "E350.visualSharp", {"position": v(4.24, 0) * mm});
            skArc(sketch, "E350.filletArc", {"start": v(4.95, 0.7) * mm, "mid": v(4.66, 0) * mm, "end": v(4.95, -0.7) * mm});
            skPoint(sketch, "E351.visualSharp", {"position": v(0, -4.24) * mm});
            skArc(sketch, "E351.filletArc", {"start": v(0.7, -4.95) * mm, "mid": v(0, -4.66) * mm, "end": v(-0.7, -4.95) * mm});
            skPoint(sketch, "E352.visualSharp", {"position": v(-4.24, 0) * mm});
            skArc(sketch, "E352.filletArc", {"start": v(-4.95, -0.7) * mm, "mid": v(-4.66, 0) * mm, "end": v(-4.95, 0.7) * mm});
            skPoint(sketch, "E353.visualSharp", {"position": v(-13, 8.76) * mm});
            skArc(sketch, "E353.filletArc", {"start": v(-11.3, 7.05) * mm, "mid": v(-12.38, 7.27) * mm, "end": v(-13, 6.34) * mm});
            skPoint(sketch, "E354.visualSharp", {"position": v(-13, -8.76) * mm});
            skArc(sketch, "E354.filletArc", {"start": v(-13, -6.34) * mm, "mid": v(-12.38, -7.27) * mm, "end": v(-11.3, -7.05) * mm});
            skPoint(sketch, "E355.visualSharp", {"position": v(-8.76, -13) * mm});
            skArc(sketch, "E355.filletArc", {"start": v(-7.05, -11.3) * mm, "mid": v(-7.27, -12.38) * mm, "end": v(-6.34, -13) * mm});
            skPoint(sketch, "E356.visualSharp", {"position": v(8.76, -13) * mm});
            skArc(sketch, "E356.filletArc", {"start": v(6.34, -13) * mm, "mid": v(7.27, -12.38) * mm, "end": v(7.05, -11.3) * mm});
            skLineSegment(sketch, "E357.bottom", {"start": v(-7, 18) * mm, "end": v(7, 18) * mm});
            skLineSegment(sketch, "E357.top", {"start": v(-7, 24) * mm, "end": v(7, 24) * mm});
            skLineSegment(sketch, "E357.left", {"start": v(-8, 19) * mm, "end": v(-8, 23) * mm});
            skLineSegment(sketch, "E357.right", {"start": v(8, 19) * mm, "end": v(8, 23) * mm});
            skPoint(sketch, "E357.middle", {"position": v(0, 21) * mm});
            skPoint(sketch, "E358.visualSharp", {"position": v(-8, 24) * mm});
            skArc(sketch, "E358.filletArc", {"start": v(-7, 24) * mm, "mid": v(-7.7, 23.7) * mm, "end": v(-8, 23) * mm});
            skPoint(sketch, "E359.visualSharp", {"position": v(-8, 18) * mm});
            skArc(sketch, "E359.filletArc", {"start": v(-8, 19) * mm, "mid": v(-7.7, 18.3) * mm, "end": v(-7, 18) * mm});
            skPoint(sketch, "E360.visualSharp", {"position": v(8, 18) * mm});
            skArc(sketch, "E360.filletArc", {"start": v(7, 18) * mm, "mid": v(7.7, 18.3) * mm, "end": v(8, 19) * mm});
            skPoint(sketch, "E361.visualSharp", {"position": v(8, 24) * mm});
            skArc(sketch, "E361.filletArc", {"start": v(8, 23) * mm, "mid": v(7.7, 23.7) * mm, "end": v(7, 24) * mm});
            skArc(sketch, "E362.MirrorCS", {"start": v(7, -18) * mm, "mid": v(7.7, -18.3) * mm, "end": v(8, -19) * mm});
            skArc(sketch, "E363.MirrorCS", {"start": v(-8, -19) * mm, "mid": v(-7.7, -18.3) * mm, "end": v(-7, -18) * mm});
            skArc(sketch, "E364.MirrorCS", {"start": v(-7, -24) * mm, "mid": v(-7.7, -23.7) * mm, "end": v(-8, -23) * mm});
            skArc(sketch, "E365.MirrorCS", {"start": v(8, -23) * mm, "mid": v(7.7, -23.7) * mm, "end": v(7, -24) * mm});
            skPoint(sketch, "E366.MirrorP", {"position": v(-8, -18) * mm});
            skPoint(sketch, "E367.MirrorP", {"position": v(8, -18) * mm});
            skLineSegment(sketch, "E368.MirrorCS", {"start": v(-8, -19) * mm, "end": v(-8, -23) * mm});
            skLineSegment(sketch, "E369.MirrorCS", {"start": v(8, -19) * mm, "end": v(8, -23) * mm});
            skPoint(sketch, "E370.MirrorP", {"position": v(8, -24) * mm});
            skPoint(sketch, "E371.MirrorP", {"position": v(-8, -24) * mm});
            skLineSegment(sketch, "E372.MirrorCS", {"start": v(-7, -18) * mm, "end": v(7, -18) * mm});
            skLineSegment(sketch, "E373.MirrorCS", {"start": v(-7, -24) * mm, "end": v(7, -24) * mm});
            skPoint(sketch, "E374.MirrorP", {"position": v(0, -21) * mm});
            skSolve(sketch);
        }
        {
            var Q0;
            Q0 = qSketchRegion(id + "F49", true);
            extrude(context, id + "F50", {"entities" : qUnion([Q0]), "operationType" : NewBodyOperationType.REMOVE, "oppositeDirection" : true, "depth" : 25 * mm, "offsetDistance" : 25 * mm});
        }
    });
